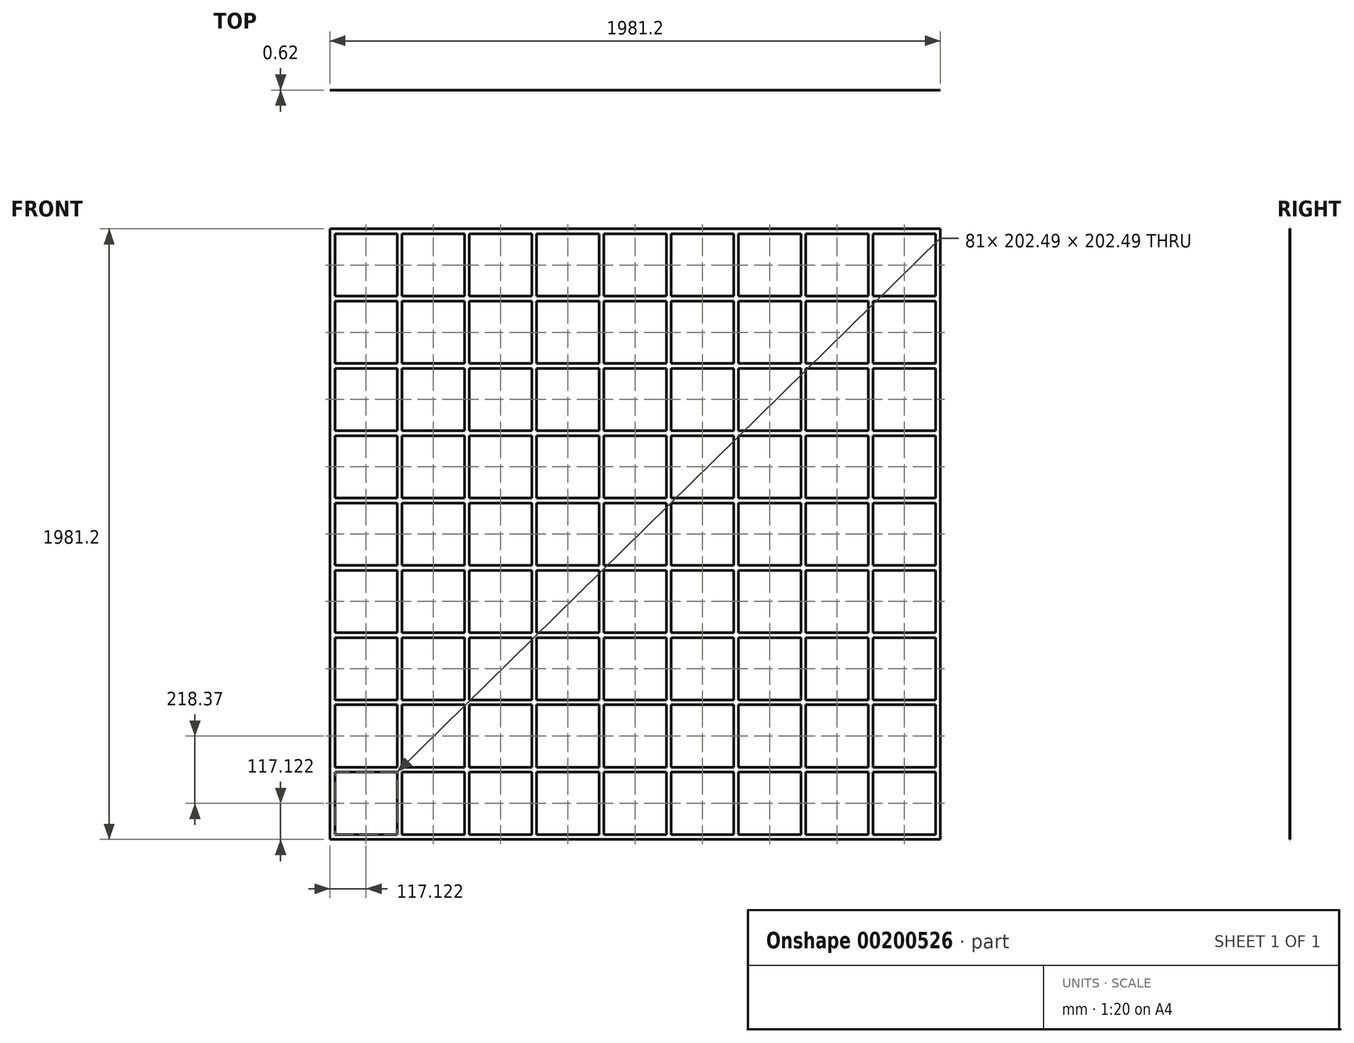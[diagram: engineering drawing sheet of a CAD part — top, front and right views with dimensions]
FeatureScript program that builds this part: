
annotation { "Feature Type Name" : "Feature", "Feature Type Description" : "" }
export const myFeature = defineFeature(function(context is Context, id is Id, definition is map)
    precondition{}
    {
        {
            assignVariable(context, id + "F0", {"name" : "Diameter", "anyValue" : 5 / 8});
        }
        {
            var Q0;
            Q0=qCreatedBy(makeId("Front.planeOp"),FACE);
            var sketch = newSketch(context, id + "F1", { "sketchPlane" : qUnion([Q0])});
            skLineSegment(sketch, "E0.bottom", {"start": v(-1066.8, 1066.8) * mm, "end": v(1066.8, 1066.8) * mm, "construction": true});
            skLineSegment(sketch, "E0.top", {"start": v(-1066.8, -1066.8) * mm, "end": v(1066.8, -1066.8) * mm, "construction": true});
            skLineSegment(sketch, "E0.left", {"start": v(-1066.8, 1066.8) * mm, "end": v(-1066.8, -1066.8) * mm, "construction": true});
            skLineSegment(sketch, "E0.right", {"start": v(1066.8, 1066.8) * mm, "end": v(1066.8, -1066.8) * mm, "construction": true});
            skLineSegment(sketch, "E1", {"start": v(1066.8, 0) * mm, "end": v(-1066.8, 0) * mm, "construction": true});
            skLineSegment(sketch, "E2", {"start": v(0, -1066.8) * mm, "end": v(0, 1066.8) * mm, "construction": true});
            skLineSegment(sketch, "E3.bottom", {"start": v(-990.6, 990.6) * mm, "end": v(990.6, 990.6) * mm, "construction": true});
            skLineSegment(sketch, "E3.top", {"start": v(-990.6, -990.6) * mm, "end": v(990.6, -990.6) * mm, "construction": true});
            skLineSegment(sketch, "E3.left", {"start": v(-990.6, 990.6) * mm, "end": v(-990.6, -990.6) * mm, "construction": true});
            skLineSegment(sketch, "E3.right", {"start": v(990.6, 990.6) * mm, "end": v(990.6, -990.6) * mm, "construction": true});
            skLineSegment(sketch, "E4.bottom", {"start": v(-990.6, 990.6) * mm, "end": v(-974.72, 990.6) * mm});
            skLineSegment(sketch, "E4.top", {"start": v(-990.6, -990.6) * mm, "end": v(-974.72, -990.6) * mm});
            skLineSegment(sketch, "E4.left", {"start": v(-990.6, 990.6) * mm, "end": v(-990.6, -990.6) * mm});
            skLineSegment(sketch, "E4.right", {"start": v(-974.72, 990.6) * mm, "end": v(-974.72, -990.6) * mm});
            skLineSegment(sketch, "E5.bottom", {"start": v(-772.23, 990.6) * mm, "end": v(-756.36, 990.6) * mm});
            skLineSegment(sketch, "E5.top", {"start": v(-772.23, -990.6) * mm, "end": v(-756.36, -990.6) * mm});
            skLineSegment(sketch, "E5.left", {"start": v(-772.23, 990.6) * mm, "end": v(-772.23, -990.6) * mm});
            skLineSegment(sketch, "E5.right", {"start": v(-756.36, 990.6) * mm, "end": v(-756.36, -990.6) * mm});
            skLineSegment(sketch, "E6.bottom", {"start": v(-553.86, 990.6) * mm, "end": v(-537.99, 990.6) * mm});
            skLineSegment(sketch, "E6.top", {"start": v(-553.86, -990.6) * mm, "end": v(-537.99, -990.6) * mm});
            skLineSegment(sketch, "E6.left", {"start": v(-553.86, 990.6) * mm, "end": v(-553.86, -990.6) * mm});
            skLineSegment(sketch, "E6.right", {"start": v(-537.99, 990.6) * mm, "end": v(-537.99, -990.6) * mm});
            skLineSegment(sketch, "E7.bottom", {"start": v(-335.5, 990.6) * mm, "end": v(-319.62, 990.6) * mm});
            skLineSegment(sketch, "E7.top", {"start": v(-335.5, -990.6) * mm, "end": v(-319.62, -990.6) * mm});
            skLineSegment(sketch, "E7.left", {"start": v(-335.5, 990.6) * mm, "end": v(-335.5, -990.6) * mm});
            skLineSegment(sketch, "E7.right", {"start": v(-319.62, 990.6) * mm, "end": v(-319.62, -990.6) * mm});
            skLineSegment(sketch, "E8.bottom", {"start": v(101.25, 990.6) * mm, "end": v(117.12, 990.6) * mm});
            skLineSegment(sketch, "E8.top", {"start": v(101.25, -990.6) * mm, "end": v(117.12, -990.6) * mm});
            skLineSegment(sketch, "E8.left", {"start": v(101.25, 990.6) * mm, "end": v(101.25, -990.6) * mm});
            skLineSegment(sketch, "E8.right", {"start": v(117.12, 990.6) * mm, "end": v(117.12, -990.6) * mm});
            skLineSegment(sketch, "E9.bottom", {"start": v(319.62, 990.6) * mm, "end": v(335.5, 990.6) * mm});
            skLineSegment(sketch, "E9.top", {"start": v(319.62, -990.6) * mm, "end": v(335.5, -990.6) * mm});
            skLineSegment(sketch, "E9.left", {"start": v(319.62, 990.6) * mm, "end": v(319.62, -990.6) * mm});
            skLineSegment(sketch, "E9.right", {"start": v(335.5, 990.6) * mm, "end": v(335.5, -990.6) * mm});
            skLineSegment(sketch, "E10.bottom", {"start": v(537.99, 990.6) * mm, "end": v(553.86, 990.6) * mm});
            skLineSegment(sketch, "E10.top", {"start": v(537.99, -990.6) * mm, "end": v(553.86, -990.6) * mm});
            skLineSegment(sketch, "E10.left", {"start": v(537.99, 990.6) * mm, "end": v(537.99, -990.6) * mm});
            skLineSegment(sketch, "E10.right", {"start": v(553.86, 990.6) * mm, "end": v(553.86, -990.6) * mm});
            skLineSegment(sketch, "E11.bottom", {"start": v(990.6, 990.6) * mm, "end": v(974.73, 990.6) * mm});
            skLineSegment(sketch, "E11.top", {"start": v(990.6, -990.6) * mm, "end": v(974.73, -990.6) * mm});
            skLineSegment(sketch, "E11.left", {"start": v(990.6, 990.6) * mm, "end": v(990.6, -990.6) * mm});
            skLineSegment(sketch, "E11.right", {"start": v(974.73, 990.6) * mm, "end": v(974.73, -990.6) * mm});
            skLineSegment(sketch, "E12.bottom", {"start": v(772.23, 990.6) * mm, "end": v(756.36, 990.6) * mm});
            skLineSegment(sketch, "E12.top", {"start": v(772.23, -990.6) * mm, "end": v(756.36, -990.6) * mm});
            skLineSegment(sketch, "E12.left", {"start": v(772.23, 990.6) * mm, "end": v(772.23, -990.6) * mm});
            skLineSegment(sketch, "E12.right", {"start": v(756.36, 990.6) * mm, "end": v(756.36, -990.6) * mm});
            skLineSegment(sketch, "E13.bottom", {"start": v(-117.12, 990.6) * mm, "end": v(-101.25, 990.6) * mm});
            skLineSegment(sketch, "E13.top", {"start": v(-117.12, -990.6) * mm, "end": v(-101.25, -990.6) * mm});
            skLineSegment(sketch, "E13.left", {"start": v(-117.12, 990.6) * mm, "end": v(-117.12, -990.6) * mm});
            skLineSegment(sketch, "E13.right", {"start": v(-101.25, 990.6) * mm, "end": v(-101.25, -990.6) * mm});
            skLineSegment(sketch, "E14.bottom", {"start": v(-990.6, 990.6) * mm, "end": v(990.6, 990.6) * mm});
            skLineSegment(sketch, "E14.top", {"start": v(-990.6, 974.72) * mm, "end": v(990.6, 974.73) * mm});
            skLineSegment(sketch, "E14.left", {"start": v(-990.6, 990.6) * mm, "end": v(-990.6, 974.72) * mm});
            skLineSegment(sketch, "E14.right", {"start": v(990.6, 990.6) * mm, "end": v(990.6, 974.73) * mm});
            skLineSegment(sketch, "E15.bottom", {"start": v(-990.6, 553.86) * mm, "end": v(990.6, 553.86) * mm});
            skLineSegment(sketch, "E15.top", {"start": v(-990.6, 537.99) * mm, "end": v(990.6, 537.99) * mm});
            skLineSegment(sketch, "E15.left", {"start": v(-990.6, 553.86) * mm, "end": v(-990.6, 537.99) * mm});
            skLineSegment(sketch, "E15.right", {"start": v(990.6, 553.86) * mm, "end": v(990.6, 537.99) * mm});
            skLineSegment(sketch, "E16.bottom", {"start": v(990.6, 756.36) * mm, "end": v(-990.6, 756.36) * mm});
            skLineSegment(sketch, "E16.top", {"start": v(990.6, 772.23) * mm, "end": v(-990.6, 772.23) * mm});
            skLineSegment(sketch, "E16.left", {"start": v(990.6, 756.36) * mm, "end": v(990.6, 772.23) * mm});
            skLineSegment(sketch, "E16.right", {"start": v(-990.6, 756.36) * mm, "end": v(-990.6, 772.23) * mm});
            skLineSegment(sketch, "E17.bottom", {"start": v(-990.6, 335.5) * mm, "end": v(990.6, 335.5) * mm});
            skLineSegment(sketch, "E17.top", {"start": v(-990.6, 319.62) * mm, "end": v(990.6, 319.62) * mm});
            skLineSegment(sketch, "E17.left", {"start": v(-990.6, 335.5) * mm, "end": v(-990.6, 319.62) * mm});
            skLineSegment(sketch, "E17.right", {"start": v(990.6, 335.5) * mm, "end": v(990.6, 319.62) * mm});
            skLineSegment(sketch, "E18.bottom", {"start": v(-990.6, 117.12) * mm, "end": v(990.6, 117.12) * mm});
            skLineSegment(sketch, "E18.top", {"start": v(-990.6, 101.25) * mm, "end": v(990.6, 101.25) * mm});
            skLineSegment(sketch, "E18.left", {"start": v(-990.6, 117.12) * mm, "end": v(-990.6, 101.25) * mm});
            skLineSegment(sketch, "E18.right", {"start": v(990.6, 117.12) * mm, "end": v(990.6, 101.25) * mm});
            skLineSegment(sketch, "E19.bottom", {"start": v(-990.6, -101.25) * mm, "end": v(990.6, -101.25) * mm});
            skLineSegment(sketch, "E19.top", {"start": v(-990.6, -117.12) * mm, "end": v(990.6, -117.12) * mm});
            skLineSegment(sketch, "E19.left", {"start": v(-990.6, -101.25) * mm, "end": v(-990.6, -117.12) * mm});
            skLineSegment(sketch, "E19.right", {"start": v(990.6, -101.25) * mm, "end": v(990.6, -117.12) * mm});
            skLineSegment(sketch, "E20.bottom", {"start": v(990.6, -319.62) * mm, "end": v(-990.6, -319.62) * mm});
            skLineSegment(sketch, "E20.top", {"start": v(990.6, -335.5) * mm, "end": v(-990.6, -335.5) * mm});
            skLineSegment(sketch, "E20.left", {"start": v(990.6, -319.62) * mm, "end": v(990.6, -335.5) * mm});
            skLineSegment(sketch, "E20.right", {"start": v(-990.6, -319.62) * mm, "end": v(-990.6, -335.5) * mm});
            skLineSegment(sketch, "E21.bottom", {"start": v(-990.6, -537.99) * mm, "end": v(990.6, -537.99) * mm});
            skLineSegment(sketch, "E21.top", {"start": v(-990.6, -553.86) * mm, "end": v(990.6, -553.86) * mm});
            skLineSegment(sketch, "E21.left", {"start": v(-990.6, -537.99) * mm, "end": v(-990.6, -553.86) * mm});
            skLineSegment(sketch, "E21.right", {"start": v(990.6, -537.99) * mm, "end": v(990.6, -553.86) * mm});
            skLineSegment(sketch, "E22.bottom", {"start": v(990.6, -756.36) * mm, "end": v(-990.6, -756.36) * mm});
            skLineSegment(sketch, "E22.top", {"start": v(990.6, -772.23) * mm, "end": v(-990.6, -772.23) * mm});
            skLineSegment(sketch, "E22.left", {"start": v(990.6, -756.36) * mm, "end": v(990.6, -772.23) * mm});
            skLineSegment(sketch, "E22.right", {"start": v(-990.6, -756.36) * mm, "end": v(-990.6, -772.23) * mm});
            skLineSegment(sketch, "E23.bottom", {"start": v(-990.6, -990.6) * mm, "end": v(990.6, -990.6) * mm});
            skLineSegment(sketch, "E23.top", {"start": v(-990.6, -974.73) * mm, "end": v(990.6, -974.72) * mm});
            skLineSegment(sketch, "E23.left", {"start": v(-990.6, -990.6) * mm, "end": v(-990.6, -974.73) * mm});
            skLineSegment(sketch, "E23.right", {"start": v(990.6, -990.6) * mm, "end": v(990.6, -974.72) * mm});
            skSolve(sketch);
        }
        {
            var Q0;
            Q0 = qSketchRegion(id + "F1", true);
            var Q1;
            {var subQ0=sQuery(id+"F1.wireOp",EDGE,"E19.bottom");var subQ1=sQuery(id+"F1.wireOp",EDGE,"E4.right");var subQ2=makeQuery(id+"F1.imprint","INTERSECT",VERTEX,{"derivedFrom":[subQ1,subQ0]});Q1=makeQuery(id+"F1.imprint","IMPRINT",FACE,{"disambiguationData":[TD([[makeQuery(id+"F1.imprint","IMPRINT",EDGE,{"disambiguationData":[TD([[subQ2,-1.0]])],"derivedFrom":subQ1}),1.0]])]});}
            var Q2;
            {var subQ0=sQuery(id+"F1.wireOp",EDGE,"E20.bottom");var subQ1=sQuery(id+"F1.wireOp",EDGE,"E4.right");var subQ2=makeQuery(id+"F1.imprint","INTERSECT",VERTEX,{"derivedFrom":[subQ1,subQ0]});Q2=makeQuery(id+"F1.imprint","IMPRINT",FACE,{"disambiguationData":[TD([[makeQuery(id+"F1.imprint","IMPRINT",EDGE,{"disambiguationData":[TD([[subQ2,-1.0]])],"derivedFrom":subQ1}),1.0]])]});}
            var Q3;
            {var subQ0=sQuery(id+"F1.wireOp",EDGE,"E21.bottom");var subQ1=sQuery(id+"F1.wireOp",EDGE,"E4.right");var subQ2=makeQuery(id+"F1.imprint","INTERSECT",VERTEX,{"derivedFrom":[subQ1,subQ0]});Q3=makeQuery(id+"F1.imprint","IMPRINT",FACE,{"disambiguationData":[TD([[makeQuery(id+"F1.imprint","IMPRINT",EDGE,{"disambiguationData":[TD([[subQ2,-1.0]])],"derivedFrom":subQ1}),1.0]])]});}
            var Q4;
            {var subQ0=sQuery(id+"F1.wireOp",EDGE,"E22.bottom");var subQ1=sQuery(id+"F1.wireOp",EDGE,"E4.right");var subQ2=makeQuery(id+"F1.imprint","INTERSECT",VERTEX,{"derivedFrom":[subQ1,subQ0]});Q4=makeQuery(id+"F1.imprint","IMPRINT",FACE,{"disambiguationData":[TD([[makeQuery(id+"F1.imprint","IMPRINT",EDGE,{"disambiguationData":[TD([[subQ2,-1.0]])],"derivedFrom":subQ1}),1.0]])]});}
            var Q5;
            {var subQ0=sQuery(id+"F1.wireOp",EDGE,"E22.top");var subQ1=sQuery(id+"F1.wireOp",EDGE,"E5.left");var subQ2=makeQuery(id+"F1.imprint","INTERSECT",VERTEX,{"derivedFrom":[subQ1,subQ0]});Q5=makeQuery(id+"F1.imprint","IMPRINT",FACE,{"disambiguationData":[TD([[makeQuery(id+"F1.imprint","IMPRINT",EDGE,{"disambiguationData":[TD([[subQ2,-1.0]])],"derivedFrom":subQ1}),1.0]])]});}
            var Q6;
            {var subQ0=sQuery(id+"F1.wireOp",EDGE,"E22.top");var subQ1=sQuery(id+"F1.wireOp",EDGE,"E6.left");var subQ2=makeQuery(id+"F1.imprint","INTERSECT",VERTEX,{"derivedFrom":[subQ1,subQ0]});Q6=makeQuery(id+"F1.imprint","IMPRINT",FACE,{"disambiguationData":[TD([[makeQuery(id+"F1.imprint","IMPRINT",EDGE,{"disambiguationData":[TD([[subQ2,-1.0]])],"derivedFrom":subQ1}),1.0]])]});}
            var Q7;
            {var subQ0=sQuery(id+"F1.wireOp",EDGE,"E21.top");var subQ1=sQuery(id+"F1.wireOp",EDGE,"E6.left");var subQ2=makeQuery(id+"F1.imprint","INTERSECT",VERTEX,{"derivedFrom":[subQ1,subQ0]});Q7=makeQuery(id+"F1.imprint","IMPRINT",FACE,{"disambiguationData":[TD([[makeQuery(id+"F1.imprint","IMPRINT",EDGE,{"disambiguationData":[TD([[subQ2,-1.0]])],"derivedFrom":subQ1}),1.0]])]});}
            var Q8;
            {var subQ0=sQuery(id+"F1.wireOp",EDGE,"E22.bottom");var subQ1=sQuery(id+"F1.wireOp",EDGE,"E5.right");var subQ2=makeQuery(id+"F1.imprint","INTERSECT",VERTEX,{"derivedFrom":[subQ1,subQ0]});Q8=makeQuery(id+"F1.imprint","IMPRINT",FACE,{"disambiguationData":[TD([[makeQuery(id+"F1.imprint","IMPRINT",EDGE,{"disambiguationData":[TD([[subQ2,-1.0]])],"derivedFrom":subQ1}),1.0]])]});}
            var Q9;
            {var subQ0=sQuery(id+"F1.wireOp",EDGE,"E21.top");var subQ1=sQuery(id+"F1.wireOp",EDGE,"E5.left");var subQ2=makeQuery(id+"F1.imprint","INTERSECT",VERTEX,{"derivedFrom":[subQ1,subQ0]});Q9=makeQuery(id+"F1.imprint","IMPRINT",FACE,{"disambiguationData":[TD([[makeQuery(id+"F1.imprint","IMPRINT",EDGE,{"disambiguationData":[TD([[subQ2,-1.0]])],"derivedFrom":subQ1}),1.0]])]});}
            var Q10;
            {var subQ0=sQuery(id+"F1.wireOp",EDGE,"E20.top");var subQ1=sQuery(id+"F1.wireOp",EDGE,"E5.left");var subQ2=makeQuery(id+"F1.imprint","INTERSECT",VERTEX,{"derivedFrom":[subQ1,subQ0]});Q10=makeQuery(id+"F1.imprint","IMPRINT",FACE,{"disambiguationData":[TD([[makeQuery(id+"F1.imprint","IMPRINT",EDGE,{"disambiguationData":[TD([[subQ2,-1.0]])],"derivedFrom":subQ1}),1.0]])]});}
            var Q11;
            {var subQ0=sQuery(id+"F1.wireOp",EDGE,"E19.top");var subQ1=sQuery(id+"F1.wireOp",EDGE,"E5.left");var subQ2=makeQuery(id+"F1.imprint","INTERSECT",VERTEX,{"derivedFrom":[subQ1,subQ0]});Q11=makeQuery(id+"F1.imprint","IMPRINT",FACE,{"disambiguationData":[TD([[makeQuery(id+"F1.imprint","IMPRINT",EDGE,{"disambiguationData":[TD([[subQ2,-1.0]])],"derivedFrom":subQ1}),1.0]])]});}
            var Q12;
            {var subQ0=sQuery(id+"F1.wireOp",EDGE,"E17.top");var subQ1=sQuery(id+"F1.wireOp",EDGE,"E5.left");var subQ2=makeQuery(id+"F1.imprint","INTERSECT",VERTEX,{"derivedFrom":[subQ1,subQ0]});Q12=makeQuery(id+"F1.imprint","IMPRINT",FACE,{"disambiguationData":[TD([[makeQuery(id+"F1.imprint","IMPRINT",EDGE,{"disambiguationData":[TD([[subQ2,-1.0]])],"derivedFrom":subQ1}),1.0]])]});}
            var Q13;
            {var subQ0=sQuery(id+"F1.wireOp",EDGE,"E15.top");var subQ1=sQuery(id+"F1.wireOp",EDGE,"E5.left");var subQ2=makeQuery(id+"F1.imprint","INTERSECT",VERTEX,{"derivedFrom":[subQ1,subQ0]});Q13=makeQuery(id+"F1.imprint","IMPRINT",FACE,{"disambiguationData":[TD([[makeQuery(id+"F1.imprint","IMPRINT",EDGE,{"disambiguationData":[TD([[subQ2,-1.0]])],"derivedFrom":subQ1}),1.0]])]});}
            var Q14;
            {var subQ0=sQuery(id+"F1.wireOp",EDGE,"E18.bottom");var subQ1=sQuery(id+"F1.wireOp",EDGE,"E4.right");var subQ2=makeQuery(id+"F1.imprint","INTERSECT",VERTEX,{"derivedFrom":[subQ1,subQ0]});Q14=makeQuery(id+"F1.imprint","IMPRINT",FACE,{"disambiguationData":[TD([[makeQuery(id+"F1.imprint","IMPRINT",EDGE,{"disambiguationData":[TD([[subQ2,-1.0]])],"derivedFrom":subQ1}),1.0]])]});}
            var Q15;
            {var subQ0=sQuery(id+"F1.wireOp",EDGE,"E18.top");var subQ1=sQuery(id+"F1.wireOp",EDGE,"E5.left");var subQ2=makeQuery(id+"F1.imprint","INTERSECT",VERTEX,{"derivedFrom":[subQ1,subQ0]});Q15=makeQuery(id+"F1.imprint","IMPRINT",FACE,{"disambiguationData":[TD([[makeQuery(id+"F1.imprint","IMPRINT",EDGE,{"disambiguationData":[TD([[subQ2,-1.0]])],"derivedFrom":subQ1}),1.0]])]});}
            var Q16;
            {var subQ0=sQuery(id+"F1.wireOp",EDGE,"E18.bottom");var subQ1=sQuery(id+"F1.wireOp",EDGE,"E5.right");var subQ2=makeQuery(id+"F1.imprint","INTERSECT",VERTEX,{"derivedFrom":[subQ1,subQ0]});Q16=makeQuery(id+"F1.imprint","IMPRINT",FACE,{"disambiguationData":[TD([[makeQuery(id+"F1.imprint","IMPRINT",EDGE,{"disambiguationData":[TD([[subQ2,-1.0]])],"derivedFrom":subQ1}),1.0]])]});}
            var Q17;
            {var subQ0=sQuery(id+"F1.wireOp",EDGE,"E18.bottom");var subQ1=sQuery(id+"F1.wireOp",EDGE,"E6.right");var subQ2=makeQuery(id+"F1.imprint","INTERSECT",VERTEX,{"derivedFrom":[subQ1,subQ0]});Q17=makeQuery(id+"F1.imprint","IMPRINT",FACE,{"disambiguationData":[TD([[makeQuery(id+"F1.imprint","IMPRINT",EDGE,{"disambiguationData":[TD([[subQ2,-1.0]])],"derivedFrom":subQ1}),1.0]])]});}
            var Q18;
            {var subQ0=sQuery(id+"F1.wireOp",EDGE,"E17.top");var subQ1=sQuery(id+"F1.wireOp",EDGE,"E6.left");var subQ2=makeQuery(id+"F1.imprint","INTERSECT",VERTEX,{"derivedFrom":[subQ1,subQ0]});Q18=makeQuery(id+"F1.imprint","IMPRINT",FACE,{"disambiguationData":[TD([[makeQuery(id+"F1.imprint","IMPRINT",EDGE,{"disambiguationData":[TD([[subQ2,-1.0]])],"derivedFrom":subQ1}),1.0]])]});}
            var Q19;
            {var subQ0=sQuery(id+"F1.wireOp",EDGE,"E18.top");var subQ1=sQuery(id+"F1.wireOp",EDGE,"E6.left");var subQ2=makeQuery(id+"F1.imprint","INTERSECT",VERTEX,{"derivedFrom":[subQ1,subQ0]});Q19=makeQuery(id+"F1.imprint","IMPRINT",FACE,{"disambiguationData":[TD([[makeQuery(id+"F1.imprint","IMPRINT",EDGE,{"disambiguationData":[TD([[subQ2,-1.0]])],"derivedFrom":subQ1}),1.0]])]});}
            var Q20;
            {var subQ0=sQuery(id+"F1.wireOp",EDGE,"E18.bottom");var subQ1=sQuery(id+"F1.wireOp",EDGE,"E6.left");var subQ2=makeQuery(id+"F1.imprint","INTERSECT",VERTEX,{"derivedFrom":[subQ1,subQ0]});Q20=makeQuery(id+"F1.imprint","IMPRINT",FACE,{"disambiguationData":[TD([[makeQuery(id+"F1.imprint","IMPRINT",EDGE,{"disambiguationData":[TD([[subQ2,-1.0]])],"derivedFrom":subQ1}),1.0]])]});}
            var Q21;
            {var subQ0=sQuery(id+"F1.wireOp",EDGE,"E18.bottom");var subQ1=sQuery(id+"F1.wireOp",EDGE,"E5.left");var subQ2=makeQuery(id+"F1.imprint","INTERSECT",VERTEX,{"derivedFrom":[subQ1,subQ0]});Q21=makeQuery(id+"F1.imprint","IMPRINT",FACE,{"disambiguationData":[TD([[makeQuery(id+"F1.imprint","IMPRINT",EDGE,{"disambiguationData":[TD([[subQ2,-1.0]])],"derivedFrom":subQ1}),1.0]])]});}
            var Q22;
            {var subQ0=sQuery(id+"F1.wireOp",EDGE,"E19.bottom");var subQ1=sQuery(id+"F1.wireOp",EDGE,"E5.left");var subQ2=makeQuery(id+"F1.imprint","INTERSECT",VERTEX,{"derivedFrom":[subQ1,subQ0]});Q22=makeQuery(id+"F1.imprint","IMPRINT",FACE,{"disambiguationData":[TD([[makeQuery(id+"F1.imprint","IMPRINT",EDGE,{"disambiguationData":[TD([[subQ2,-1.0]])],"derivedFrom":subQ1}),1.0]])]});}
            var Q23;
            {var subQ0=sQuery(id+"F1.wireOp",EDGE,"E17.bottom");var subQ1=sQuery(id+"F1.wireOp",EDGE,"E5.left");var subQ2=makeQuery(id+"F1.imprint","INTERSECT",VERTEX,{"derivedFrom":[subQ1,subQ0]});Q23=makeQuery(id+"F1.imprint","IMPRINT",FACE,{"disambiguationData":[TD([[makeQuery(id+"F1.imprint","IMPRINT",EDGE,{"disambiguationData":[TD([[subQ2,-1.0]])],"derivedFrom":subQ1}),1.0]])]});}
            var Q24;
            {var subQ0=sQuery(id+"F1.wireOp",EDGE,"E17.bottom");var subQ1=sQuery(id+"F1.wireOp",EDGE,"E6.left");var subQ2=makeQuery(id+"F1.imprint","INTERSECT",VERTEX,{"derivedFrom":[subQ1,subQ0]});Q24=makeQuery(id+"F1.imprint","IMPRINT",FACE,{"disambiguationData":[TD([[makeQuery(id+"F1.imprint","IMPRINT",EDGE,{"disambiguationData":[TD([[subQ2,-1.0]])],"derivedFrom":subQ1}),1.0]])]});}
            var Q25;
            {var subQ0=sQuery(id+"F1.wireOp",EDGE,"E17.bottom");var subQ1=sQuery(id+"F1.wireOp",EDGE,"E7.left");var subQ2=makeQuery(id+"F1.imprint","INTERSECT",VERTEX,{"derivedFrom":[subQ1,subQ0]});Q25=makeQuery(id+"F1.imprint","IMPRINT",FACE,{"disambiguationData":[TD([[makeQuery(id+"F1.imprint","IMPRINT",EDGE,{"disambiguationData":[TD([[subQ2,-1.0]])],"derivedFrom":subQ1}),1.0]])]});}
            var Q26;
            {var subQ0=sQuery(id+"F1.wireOp",EDGE,"E17.top");var subQ1=sQuery(id+"F1.wireOp",EDGE,"E7.left");var subQ2=makeQuery(id+"F1.imprint","INTERSECT",VERTEX,{"derivedFrom":[subQ1,subQ0]});Q26=makeQuery(id+"F1.imprint","IMPRINT",FACE,{"disambiguationData":[TD([[makeQuery(id+"F1.imprint","IMPRINT",EDGE,{"disambiguationData":[TD([[subQ2,-1.0]])],"derivedFrom":subQ1}),1.0]])]});}
            var Q27;
            {var subQ0=sQuery(id+"F1.wireOp",EDGE,"E18.bottom");var subQ1=sQuery(id+"F1.wireOp",EDGE,"E7.left");var subQ2=makeQuery(id+"F1.imprint","INTERSECT",VERTEX,{"derivedFrom":[subQ1,subQ0]});Q27=makeQuery(id+"F1.imprint","IMPRINT",FACE,{"disambiguationData":[TD([[makeQuery(id+"F1.imprint","IMPRINT",EDGE,{"disambiguationData":[TD([[subQ2,-1.0]])],"derivedFrom":subQ1}),1.0]])]});}
            var Q28;
            {var subQ0=sQuery(id+"F1.wireOp",EDGE,"E18.top");var subQ1=sQuery(id+"F1.wireOp",EDGE,"E7.left");var subQ2=makeQuery(id+"F1.imprint","INTERSECT",VERTEX,{"derivedFrom":[subQ1,subQ0]});Q28=makeQuery(id+"F1.imprint","IMPRINT",FACE,{"disambiguationData":[TD([[makeQuery(id+"F1.imprint","IMPRINT",EDGE,{"disambiguationData":[TD([[subQ2,-1.0]])],"derivedFrom":subQ1}),1.0]])]});}
            var Q29;
            {var subQ0=sQuery(id+"F1.wireOp",EDGE,"E19.bottom");var subQ1=sQuery(id+"F1.wireOp",EDGE,"E7.left");var subQ2=makeQuery(id+"F1.imprint","INTERSECT",VERTEX,{"derivedFrom":[subQ1,subQ0]});Q29=makeQuery(id+"F1.imprint","IMPRINT",FACE,{"disambiguationData":[TD([[makeQuery(id+"F1.imprint","IMPRINT",EDGE,{"disambiguationData":[TD([[subQ2,-1.0]])],"derivedFrom":subQ1}),1.0]])]});}
            var Q30;
            {var subQ0=sQuery(id+"F1.wireOp",EDGE,"E19.bottom");var subQ1=sQuery(id+"F1.wireOp",EDGE,"E6.right");var subQ2=makeQuery(id+"F1.imprint","INTERSECT",VERTEX,{"derivedFrom":[subQ1,subQ0]});Q30=makeQuery(id+"F1.imprint","IMPRINT",FACE,{"disambiguationData":[TD([[makeQuery(id+"F1.imprint","IMPRINT",EDGE,{"disambiguationData":[TD([[subQ2,-1.0]])],"derivedFrom":subQ1}),1.0]])]});}
            var Q31;
            {var subQ0=sQuery(id+"F1.wireOp",EDGE,"E19.bottom");var subQ1=sQuery(id+"F1.wireOp",EDGE,"E6.left");var subQ2=makeQuery(id+"F1.imprint","INTERSECT",VERTEX,{"derivedFrom":[subQ1,subQ0]});Q31=makeQuery(id+"F1.imprint","IMPRINT",FACE,{"disambiguationData":[TD([[makeQuery(id+"F1.imprint","IMPRINT",EDGE,{"disambiguationData":[TD([[subQ2,-1.0]])],"derivedFrom":subQ1}),1.0]])]});}
            var Q32;
            {var subQ0=sQuery(id+"F1.wireOp",EDGE,"E19.bottom");var subQ1=sQuery(id+"F1.wireOp",EDGE,"E5.right");var subQ2=makeQuery(id+"F1.imprint","INTERSECT",VERTEX,{"derivedFrom":[subQ1,subQ0]});Q32=makeQuery(id+"F1.imprint","IMPRINT",FACE,{"disambiguationData":[TD([[makeQuery(id+"F1.imprint","IMPRINT",EDGE,{"disambiguationData":[TD([[subQ2,-1.0]])],"derivedFrom":subQ1}),1.0]])]});}
            var Q33;
            {var subQ0=sQuery(id+"F1.wireOp",EDGE,"E19.top");var subQ1=sQuery(id+"F1.wireOp",EDGE,"E6.left");var subQ2=makeQuery(id+"F1.imprint","INTERSECT",VERTEX,{"derivedFrom":[subQ1,subQ0]});Q33=makeQuery(id+"F1.imprint","IMPRINT",FACE,{"disambiguationData":[TD([[makeQuery(id+"F1.imprint","IMPRINT",EDGE,{"disambiguationData":[TD([[subQ2,-1.0]])],"derivedFrom":subQ1}),1.0]])]});}
            var Q34;
            {var subQ0=sQuery(id+"F1.wireOp",EDGE,"E17.bottom");var subQ1=sQuery(id+"F1.wireOp",EDGE,"E4.right");var subQ2=makeQuery(id+"F1.imprint","INTERSECT",VERTEX,{"derivedFrom":[subQ1,subQ0]});Q34=makeQuery(id+"F1.imprint","IMPRINT",FACE,{"disambiguationData":[TD([[makeQuery(id+"F1.imprint","IMPRINT",EDGE,{"disambiguationData":[TD([[subQ2,-1.0]])],"derivedFrom":subQ1}),1.0]])]});}
            var Q35;
            {var subQ0=sQuery(id+"F1.wireOp",EDGE,"E17.bottom");var subQ1=sQuery(id+"F1.wireOp",EDGE,"E5.right");var subQ2=makeQuery(id+"F1.imprint","INTERSECT",VERTEX,{"derivedFrom":[subQ1,subQ0]});Q35=makeQuery(id+"F1.imprint","IMPRINT",FACE,{"disambiguationData":[TD([[makeQuery(id+"F1.imprint","IMPRINT",EDGE,{"disambiguationData":[TD([[subQ2,-1.0]])],"derivedFrom":subQ1}),1.0]])]});}
            var Q36;
            {var subQ0=sQuery(id+"F1.wireOp",EDGE,"E15.top");var subQ1=sQuery(id+"F1.wireOp",EDGE,"E6.left");var subQ2=makeQuery(id+"F1.imprint","INTERSECT",VERTEX,{"derivedFrom":[subQ1,subQ0]});Q36=makeQuery(id+"F1.imprint","IMPRINT",FACE,{"disambiguationData":[TD([[makeQuery(id+"F1.imprint","IMPRINT",EDGE,{"disambiguationData":[TD([[subQ2,-1.0]])],"derivedFrom":subQ1}),1.0]])]});}
            var Q37;
            {var subQ0=sQuery(id+"F1.wireOp",EDGE,"E17.bottom");var subQ1=sQuery(id+"F1.wireOp",EDGE,"E6.right");var subQ2=makeQuery(id+"F1.imprint","INTERSECT",VERTEX,{"derivedFrom":[subQ1,subQ0]});Q37=makeQuery(id+"F1.imprint","IMPRINT",FACE,{"disambiguationData":[TD([[makeQuery(id+"F1.imprint","IMPRINT",EDGE,{"disambiguationData":[TD([[subQ2,-1.0]])],"derivedFrom":subQ1}),1.0]])]});}
            var Q38;
            {var subQ0=sQuery(id+"F1.wireOp",EDGE,"E15.top");var subQ1=sQuery(id+"F1.wireOp",EDGE,"E7.left");var subQ2=makeQuery(id+"F1.imprint","INTERSECT",VERTEX,{"derivedFrom":[subQ1,subQ0]});Q38=makeQuery(id+"F1.imprint","IMPRINT",FACE,{"disambiguationData":[TD([[makeQuery(id+"F1.imprint","IMPRINT",EDGE,{"disambiguationData":[TD([[subQ2,-1.0]])],"derivedFrom":subQ1}),1.0]])]});}
            var Q39;
            {var subQ0=sQuery(id+"F1.wireOp",EDGE,"E15.bottom");var subQ1=sQuery(id+"F1.wireOp",EDGE,"E7.left");var subQ2=makeQuery(id+"F1.imprint","INTERSECT",VERTEX,{"derivedFrom":[subQ1,subQ0]});Q39=makeQuery(id+"F1.imprint","IMPRINT",FACE,{"disambiguationData":[TD([[makeQuery(id+"F1.imprint","IMPRINT",EDGE,{"disambiguationData":[TD([[subQ2,-1.0]])],"derivedFrom":subQ1}),1.0]])]});}
            var Q40;
            {var subQ0=sQuery(id+"F1.wireOp",EDGE,"E15.bottom");var subQ1=sQuery(id+"F1.wireOp",EDGE,"E6.right");var subQ2=makeQuery(id+"F1.imprint","INTERSECT",VERTEX,{"derivedFrom":[subQ1,subQ0]});Q40=makeQuery(id+"F1.imprint","IMPRINT",FACE,{"disambiguationData":[TD([[makeQuery(id+"F1.imprint","IMPRINT",EDGE,{"disambiguationData":[TD([[subQ2,-1.0]])],"derivedFrom":subQ1}),1.0]])]});}
            var Q41;
            {var subQ0=sQuery(id+"F1.wireOp",EDGE,"E15.bottom");var subQ1=sQuery(id+"F1.wireOp",EDGE,"E6.left");var subQ2=makeQuery(id+"F1.imprint","INTERSECT",VERTEX,{"derivedFrom":[subQ1,subQ0]});Q41=makeQuery(id+"F1.imprint","IMPRINT",FACE,{"disambiguationData":[TD([[makeQuery(id+"F1.imprint","IMPRINT",EDGE,{"disambiguationData":[TD([[subQ2,-1.0]])],"derivedFrom":subQ1}),1.0]])]});}
            var Q42;
            {var subQ0=sQuery(id+"F1.wireOp",EDGE,"E15.bottom");var subQ1=sQuery(id+"F1.wireOp",EDGE,"E5.right");var subQ2=makeQuery(id+"F1.imprint","INTERSECT",VERTEX,{"derivedFrom":[subQ1,subQ0]});Q42=makeQuery(id+"F1.imprint","IMPRINT",FACE,{"disambiguationData":[TD([[makeQuery(id+"F1.imprint","IMPRINT",EDGE,{"disambiguationData":[TD([[subQ2,-1.0]])],"derivedFrom":subQ1}),1.0]])]});}
            var Q43;
            {var subQ0=sQuery(id+"F1.wireOp",EDGE,"E15.bottom");var subQ1=sQuery(id+"F1.wireOp",EDGE,"E4.right");var subQ2=makeQuery(id+"F1.imprint","INTERSECT",VERTEX,{"derivedFrom":[subQ1,subQ0]});Q43=makeQuery(id+"F1.imprint","IMPRINT",FACE,{"disambiguationData":[TD([[makeQuery(id+"F1.imprint","IMPRINT",EDGE,{"disambiguationData":[TD([[subQ2,-1.0]])],"derivedFrom":subQ1}),1.0]])]});}
            var Q44;
            {var subQ0=sQuery(id+"F1.wireOp",EDGE,"E15.bottom");var subQ1=sQuery(id+"F1.wireOp",EDGE,"E5.left");var subQ2=makeQuery(id+"F1.imprint","INTERSECT",VERTEX,{"derivedFrom":[subQ1,subQ0]});Q44=makeQuery(id+"F1.imprint","IMPRINT",FACE,{"disambiguationData":[TD([[makeQuery(id+"F1.imprint","IMPRINT",EDGE,{"disambiguationData":[TD([[subQ2,-1.0]])],"derivedFrom":subQ1}),1.0]])]});}
            var Q45;
            {var subQ0=sQuery(id+"F1.wireOp",EDGE,"E16.bottom");var subQ1=sQuery(id+"F1.wireOp",EDGE,"E5.left");var subQ2=makeQuery(id+"F1.imprint","INTERSECT",VERTEX,{"derivedFrom":[subQ1,subQ0]});Q45=makeQuery(id+"F1.imprint","IMPRINT",FACE,{"disambiguationData":[TD([[makeQuery(id+"F1.imprint","IMPRINT",EDGE,{"disambiguationData":[TD([[subQ2,-1.0]])],"derivedFrom":subQ1}),1.0]])]});}
            var Q46;
            {var subQ0=sQuery(id+"F1.wireOp",EDGE,"E16.bottom");var subQ1=sQuery(id+"F1.wireOp",EDGE,"E6.left");var subQ2=makeQuery(id+"F1.imprint","INTERSECT",VERTEX,{"derivedFrom":[subQ1,subQ0]});Q46=makeQuery(id+"F1.imprint","IMPRINT",FACE,{"disambiguationData":[TD([[makeQuery(id+"F1.imprint","IMPRINT",EDGE,{"disambiguationData":[TD([[subQ2,-1.0]])],"derivedFrom":subQ1}),1.0]])]});}
            var Q47;
            {var subQ0=sQuery(id+"F1.wireOp",EDGE,"E16.bottom");var subQ1=sQuery(id+"F1.wireOp",EDGE,"E7.left");var subQ2=makeQuery(id+"F1.imprint","INTERSECT",VERTEX,{"derivedFrom":[subQ1,subQ0]});Q47=makeQuery(id+"F1.imprint","IMPRINT",FACE,{"disambiguationData":[TD([[makeQuery(id+"F1.imprint","IMPRINT",EDGE,{"disambiguationData":[TD([[subQ2,-1.0]])],"derivedFrom":subQ1}),1.0]])]});}
            var Q48;
            {var subQ0=sQuery(id+"F1.wireOp",EDGE,"E15.bottom");var subQ1=sQuery(id+"F1.wireOp",EDGE,"E7.right");var subQ2=makeQuery(id+"F1.imprint","INTERSECT",VERTEX,{"derivedFrom":[subQ1,subQ0]});Q48=makeQuery(id+"F1.imprint","IMPRINT",FACE,{"disambiguationData":[TD([[makeQuery(id+"F1.imprint","IMPRINT",EDGE,{"disambiguationData":[TD([[subQ2,-1.0]])],"derivedFrom":subQ1}),1.0]])]});}
            var Q49;
            {var subQ0=sQuery(id+"F1.wireOp",EDGE,"E17.bottom");var subQ1=sQuery(id+"F1.wireOp",EDGE,"E7.right");var subQ2=makeQuery(id+"F1.imprint","INTERSECT",VERTEX,{"derivedFrom":[subQ1,subQ0]});Q49=makeQuery(id+"F1.imprint","IMPRINT",FACE,{"disambiguationData":[TD([[makeQuery(id+"F1.imprint","IMPRINT",EDGE,{"disambiguationData":[TD([[subQ2,-1.0]])],"derivedFrom":subQ1}),1.0]])]});}
            var Q50;
            {var subQ0=sQuery(id+"F1.wireOp",EDGE,"E18.bottom");var subQ1=sQuery(id+"F1.wireOp",EDGE,"E7.right");var subQ2=makeQuery(id+"F1.imprint","INTERSECT",VERTEX,{"derivedFrom":[subQ1,subQ0]});Q50=makeQuery(id+"F1.imprint","IMPRINT",FACE,{"disambiguationData":[TD([[makeQuery(id+"F1.imprint","IMPRINT",EDGE,{"disambiguationData":[TD([[subQ2,-1.0]])],"derivedFrom":subQ1}),1.0]])]});}
            var Q51;
            {var subQ0=sQuery(id+"F1.wireOp",EDGE,"E17.top");var subQ1=sQuery(id+"F1.wireOp",EDGE,"E13.left");var subQ2=makeQuery(id+"F1.imprint","INTERSECT",VERTEX,{"derivedFrom":[subQ1,subQ0]});Q51=makeQuery(id+"F1.imprint","IMPRINT",FACE,{"disambiguationData":[TD([[makeQuery(id+"F1.imprint","IMPRINT",EDGE,{"disambiguationData":[TD([[subQ2,-1.0]])],"derivedFrom":subQ1}),1.0]])]});}
            var Q52;
            {var subQ0=sQuery(id+"F1.wireOp",EDGE,"E18.bottom");var subQ1=sQuery(id+"F1.wireOp",EDGE,"E13.left");var subQ2=makeQuery(id+"F1.imprint","INTERSECT",VERTEX,{"derivedFrom":[subQ1,subQ0]});Q52=makeQuery(id+"F1.imprint","IMPRINT",FACE,{"disambiguationData":[TD([[makeQuery(id+"F1.imprint","IMPRINT",EDGE,{"disambiguationData":[TD([[subQ2,-1.0]])],"derivedFrom":subQ1}),1.0]])]});}
            var Q53;
            {var subQ0=sQuery(id+"F1.wireOp",EDGE,"E17.bottom");var subQ1=sQuery(id+"F1.wireOp",EDGE,"E13.left");var subQ2=makeQuery(id+"F1.imprint","INTERSECT",VERTEX,{"derivedFrom":[subQ1,subQ0]});Q53=makeQuery(id+"F1.imprint","IMPRINT",FACE,{"disambiguationData":[TD([[makeQuery(id+"F1.imprint","IMPRINT",EDGE,{"disambiguationData":[TD([[subQ2,-1.0]])],"derivedFrom":subQ1}),1.0]])]});}
            var Q54;
            {var subQ0=sQuery(id+"F1.wireOp",EDGE,"E15.bottom");var subQ1=sQuery(id+"F1.wireOp",EDGE,"E13.left");var subQ2=makeQuery(id+"F1.imprint","INTERSECT",VERTEX,{"derivedFrom":[subQ1,subQ0]});Q54=makeQuery(id+"F1.imprint","IMPRINT",FACE,{"disambiguationData":[TD([[makeQuery(id+"F1.imprint","IMPRINT",EDGE,{"disambiguationData":[TD([[subQ2,-1.0]])],"derivedFrom":subQ1}),1.0]])]});}
            var Q55;
            {var subQ0=sQuery(id+"F1.wireOp",EDGE,"E16.top");var subQ1=sQuery(id+"F1.wireOp",EDGE,"E13.left");var subQ2=makeQuery(id+"F1.imprint","INTERSECT",VERTEX,{"derivedFrom":[subQ1,subQ0]});Q55=makeQuery(id+"F1.imprint","IMPRINT",FACE,{"disambiguationData":[TD([[makeQuery(id+"F1.imprint","IMPRINT",EDGE,{"disambiguationData":[TD([[subQ2,-1.0]])],"derivedFrom":subQ1}),1.0]])]});}
            var Q56;
            {var subQ0=sQuery(id+"F1.wireOp",EDGE,"E16.bottom");var subQ1=sQuery(id+"F1.wireOp",EDGE,"E13.left");var subQ2=makeQuery(id+"F1.imprint","INTERSECT",VERTEX,{"derivedFrom":[subQ1,subQ0]});Q56=makeQuery(id+"F1.imprint","IMPRINT",FACE,{"disambiguationData":[TD([[makeQuery(id+"F1.imprint","IMPRINT",EDGE,{"disambiguationData":[TD([[subQ2,-1.0]])],"derivedFrom":subQ1}),1.0]])]});}
            var Q57;
            {var subQ0=sQuery(id+"F1.wireOp",EDGE,"E16.top");var subQ1=sQuery(id+"F1.wireOp",EDGE,"E7.right");var subQ2=makeQuery(id+"F1.imprint","INTERSECT",VERTEX,{"derivedFrom":[subQ1,subQ0]});Q57=makeQuery(id+"F1.imprint","IMPRINT",FACE,{"disambiguationData":[TD([[makeQuery(id+"F1.imprint","IMPRINT",EDGE,{"disambiguationData":[TD([[subQ2,-1.0]])],"derivedFrom":subQ1}),1.0]])]});}
            var Q58;
            {var subQ0=sQuery(id+"F1.wireOp",EDGE,"E16.top");var subQ1=sQuery(id+"F1.wireOp",EDGE,"E7.left");var subQ2=makeQuery(id+"F1.imprint","INTERSECT",VERTEX,{"derivedFrom":[subQ1,subQ0]});Q58=makeQuery(id+"F1.imprint","IMPRINT",FACE,{"disambiguationData":[TD([[makeQuery(id+"F1.imprint","IMPRINT",EDGE,{"disambiguationData":[TD([[subQ2,-1.0]])],"derivedFrom":subQ1}),1.0]])]});}
            var Q59;
            {var subQ0=sQuery(id+"F1.wireOp",EDGE,"E16.top");var subQ1=sQuery(id+"F1.wireOp",EDGE,"E6.right");var subQ2=makeQuery(id+"F1.imprint","INTERSECT",VERTEX,{"derivedFrom":[subQ1,subQ0]});Q59=makeQuery(id+"F1.imprint","IMPRINT",FACE,{"disambiguationData":[TD([[makeQuery(id+"F1.imprint","IMPRINT",EDGE,{"disambiguationData":[TD([[subQ2,-1.0]])],"derivedFrom":subQ1}),1.0]])]});}
            var Q60;
            {var subQ0=sQuery(id+"F1.wireOp",EDGE,"E16.top");var subQ1=sQuery(id+"F1.wireOp",EDGE,"E6.left");var subQ2=makeQuery(id+"F1.imprint","INTERSECT",VERTEX,{"derivedFrom":[subQ1,subQ0]});Q60=makeQuery(id+"F1.imprint","IMPRINT",FACE,{"disambiguationData":[TD([[makeQuery(id+"F1.imprint","IMPRINT",EDGE,{"disambiguationData":[TD([[subQ2,-1.0]])],"derivedFrom":subQ1}),1.0]])]});}
            var Q61;
            {var subQ0=sQuery(id+"F1.wireOp",EDGE,"E16.top");var subQ1=sQuery(id+"F1.wireOp",EDGE,"E5.right");var subQ2=makeQuery(id+"F1.imprint","INTERSECT",VERTEX,{"derivedFrom":[subQ1,subQ0]});Q61=makeQuery(id+"F1.imprint","IMPRINT",FACE,{"disambiguationData":[TD([[makeQuery(id+"F1.imprint","IMPRINT",EDGE,{"disambiguationData":[TD([[subQ2,-1.0]])],"derivedFrom":subQ1}),1.0]])]});}
            var Q62;
            {var subQ0=sQuery(id+"F1.wireOp",EDGE,"E17.bottom");var subQ1=sQuery(id+"F1.wireOp",EDGE,"E8.left");var subQ2=makeQuery(id+"F1.imprint","INTERSECT",VERTEX,{"derivedFrom":[subQ1,subQ0]});Q62=makeQuery(id+"F1.imprint","IMPRINT",FACE,{"disambiguationData":[TD([[makeQuery(id+"F1.imprint","IMPRINT",EDGE,{"disambiguationData":[TD([[subQ2,-1.0]])],"derivedFrom":subQ1}),-1.0]])]});}
            var Q63;
            {var subQ0=sQuery(id+"F1.wireOp",EDGE,"E17.bottom");var subQ1=sQuery(id+"F1.wireOp",EDGE,"E8.right");var subQ2=makeQuery(id+"F1.imprint","INTERSECT",VERTEX,{"derivedFrom":[subQ1,subQ0]});Q63=makeQuery(id+"F1.imprint","IMPRINT",FACE,{"disambiguationData":[TD([[makeQuery(id+"F1.imprint","IMPRINT",EDGE,{"disambiguationData":[TD([[subQ2,-1.0]])],"derivedFrom":subQ1}),1.0]])]});}
            var Q64;
            {var subQ0=sQuery(id+"F1.wireOp",EDGE,"E17.bottom");var subQ1=sQuery(id+"F1.wireOp",EDGE,"E8.left");var subQ2=makeQuery(id+"F1.imprint","INTERSECT",VERTEX,{"derivedFrom":[subQ1,subQ0]});Q64=makeQuery(id+"F1.imprint","IMPRINT",FACE,{"disambiguationData":[TD([[makeQuery(id+"F1.imprint","IMPRINT",EDGE,{"disambiguationData":[TD([[subQ2,-1.0]])],"derivedFrom":subQ1}),1.0]])]});}
            var Q65;
            {var subQ0=sQuery(id+"F1.wireOp",EDGE,"E17.top");var subQ1=sQuery(id+"F1.wireOp",EDGE,"E8.left");var subQ2=makeQuery(id+"F1.imprint","INTERSECT",VERTEX,{"derivedFrom":[subQ1,subQ0]});Q65=makeQuery(id+"F1.imprint","IMPRINT",FACE,{"disambiguationData":[TD([[makeQuery(id+"F1.imprint","IMPRINT",EDGE,{"disambiguationData":[TD([[subQ2,-1.0]])],"derivedFrom":subQ1}),1.0]])]});}
            var Q66;
            {var subQ0=sQuery(id+"F1.wireOp",EDGE,"E18.bottom");var subQ1=sQuery(id+"F1.wireOp",EDGE,"E8.left");var subQ2=makeQuery(id+"F1.imprint","INTERSECT",VERTEX,{"derivedFrom":[subQ1,subQ0]});Q66=makeQuery(id+"F1.imprint","IMPRINT",FACE,{"disambiguationData":[TD([[makeQuery(id+"F1.imprint","IMPRINT",EDGE,{"disambiguationData":[TD([[subQ2,-1.0]])],"derivedFrom":subQ1}),1.0]])]});}
            var Q67;
            {var subQ0=sQuery(id+"F1.wireOp",EDGE,"E18.bottom");var subQ1=sQuery(id+"F1.wireOp",EDGE,"E8.left");var subQ2=makeQuery(id+"F1.imprint","INTERSECT",VERTEX,{"derivedFrom":[subQ1,subQ0]});Q67=makeQuery(id+"F1.imprint","IMPRINT",FACE,{"disambiguationData":[TD([[makeQuery(id+"F1.imprint","IMPRINT",EDGE,{"disambiguationData":[TD([[subQ2,-1.0]])],"derivedFrom":subQ1}),-1.0]])]});}
            var Q68;
            {var subQ0=sQuery(id+"F1.wireOp",EDGE,"E18.top");var subQ1=sQuery(id+"F1.wireOp",EDGE,"E8.left");var subQ2=makeQuery(id+"F1.imprint","INTERSECT",VERTEX,{"derivedFrom":[subQ1,subQ0]});Q68=makeQuery(id+"F1.imprint","IMPRINT",FACE,{"disambiguationData":[TD([[makeQuery(id+"F1.imprint","IMPRINT",EDGE,{"disambiguationData":[TD([[subQ2,-1.0]])],"derivedFrom":subQ1}),1.0]])]});}
            var Q69;
            {var subQ0=sQuery(id+"F1.wireOp",EDGE,"E18.bottom");var subQ1=sQuery(id+"F1.wireOp",EDGE,"E8.right");var subQ2=makeQuery(id+"F1.imprint","INTERSECT",VERTEX,{"derivedFrom":[subQ1,subQ0]});Q69=makeQuery(id+"F1.imprint","IMPRINT",FACE,{"disambiguationData":[TD([[makeQuery(id+"F1.imprint","IMPRINT",EDGE,{"disambiguationData":[TD([[subQ2,-1.0]])],"derivedFrom":subQ1}),1.0]])]});}
            var Q70;
            {var subQ0=sQuery(id+"F1.wireOp",EDGE,"E17.top");var subQ1=sQuery(id+"F1.wireOp",EDGE,"E9.left");var subQ2=makeQuery(id+"F1.imprint","INTERSECT",VERTEX,{"derivedFrom":[subQ1,subQ0]});Q70=makeQuery(id+"F1.imprint","IMPRINT",FACE,{"disambiguationData":[TD([[makeQuery(id+"F1.imprint","IMPRINT",EDGE,{"disambiguationData":[TD([[subQ2,-1.0]])],"derivedFrom":subQ1}),1.0]])]});}
            var Q71;
            {var subQ0=sQuery(id+"F1.wireOp",EDGE,"E18.bottom");var subQ1=sQuery(id+"F1.wireOp",EDGE,"E9.left");var subQ2=makeQuery(id+"F1.imprint","INTERSECT",VERTEX,{"derivedFrom":[subQ1,subQ0]});Q71=makeQuery(id+"F1.imprint","IMPRINT",FACE,{"disambiguationData":[TD([[makeQuery(id+"F1.imprint","IMPRINT",EDGE,{"disambiguationData":[TD([[subQ2,-1.0]])],"derivedFrom":subQ1}),1.0]])]});}
            var Q72;
            {var subQ0=sQuery(id+"F1.wireOp",EDGE,"E18.top");var subQ1=sQuery(id+"F1.wireOp",EDGE,"E9.left");var subQ2=makeQuery(id+"F1.imprint","INTERSECT",VERTEX,{"derivedFrom":[subQ1,subQ0]});Q72=makeQuery(id+"F1.imprint","IMPRINT",FACE,{"disambiguationData":[TD([[makeQuery(id+"F1.imprint","IMPRINT",EDGE,{"disambiguationData":[TD([[subQ2,-1.0]])],"derivedFrom":subQ1}),1.0]])]});}
            var Q73;
            {var subQ0=sQuery(id+"F1.wireOp",EDGE,"E18.bottom");var subQ1=sQuery(id+"F1.wireOp",EDGE,"E9.right");var subQ2=makeQuery(id+"F1.imprint","INTERSECT",VERTEX,{"derivedFrom":[subQ1,subQ0]});Q73=makeQuery(id+"F1.imprint","IMPRINT",FACE,{"disambiguationData":[TD([[makeQuery(id+"F1.imprint","IMPRINT",EDGE,{"disambiguationData":[TD([[subQ2,-1.0]])],"derivedFrom":subQ1}),1.0]])]});}
            var Q74;
            {var subQ0=sQuery(id+"F1.wireOp",EDGE,"E17.top");var subQ1=sQuery(id+"F1.wireOp",EDGE,"E10.left");var subQ2=makeQuery(id+"F1.imprint","INTERSECT",VERTEX,{"derivedFrom":[subQ1,subQ0]});Q74=makeQuery(id+"F1.imprint","IMPRINT",FACE,{"disambiguationData":[TD([[makeQuery(id+"F1.imprint","IMPRINT",EDGE,{"disambiguationData":[TD([[subQ2,-1.0]])],"derivedFrom":subQ1}),1.0]])]});}
            var Q75;
            {var subQ0=sQuery(id+"F1.wireOp",EDGE,"E18.bottom");var subQ1=sQuery(id+"F1.wireOp",EDGE,"E10.left");var subQ2=makeQuery(id+"F1.imprint","INTERSECT",VERTEX,{"derivedFrom":[subQ1,subQ0]});Q75=makeQuery(id+"F1.imprint","IMPRINT",FACE,{"disambiguationData":[TD([[makeQuery(id+"F1.imprint","IMPRINT",EDGE,{"disambiguationData":[TD([[subQ2,-1.0]])],"derivedFrom":subQ1}),1.0]])]});}
            var Q76;
            {var subQ0=sQuery(id+"F1.wireOp",EDGE,"E18.top");var subQ1=sQuery(id+"F1.wireOp",EDGE,"E10.left");var subQ2=makeQuery(id+"F1.imprint","INTERSECT",VERTEX,{"derivedFrom":[subQ1,subQ0]});Q76=makeQuery(id+"F1.imprint","IMPRINT",FACE,{"disambiguationData":[TD([[makeQuery(id+"F1.imprint","IMPRINT",EDGE,{"disambiguationData":[TD([[subQ2,-1.0]])],"derivedFrom":subQ1}),1.0]])]});}
            var Q77;
            {var subQ0=sQuery(id+"F1.wireOp",EDGE,"E18.bottom");var subQ1=sQuery(id+"F1.wireOp",EDGE,"E10.right");var subQ2=makeQuery(id+"F1.imprint","INTERSECT",VERTEX,{"derivedFrom":[subQ1,subQ0]});Q77=makeQuery(id+"F1.imprint","IMPRINT",FACE,{"disambiguationData":[TD([[makeQuery(id+"F1.imprint","IMPRINT",EDGE,{"disambiguationData":[TD([[subQ2,-1.0]])],"derivedFrom":subQ1}),1.0]])]});}
            var Q78;
            {var subQ0=sQuery(id+"F1.wireOp",EDGE,"E17.bottom");var subQ1=sQuery(id+"F1.wireOp",EDGE,"E10.right");var subQ2=makeQuery(id+"F1.imprint","INTERSECT",VERTEX,{"derivedFrom":[subQ1,subQ0]});Q78=makeQuery(id+"F1.imprint","IMPRINT",FACE,{"disambiguationData":[TD([[makeQuery(id+"F1.imprint","IMPRINT",EDGE,{"disambiguationData":[TD([[subQ2,-1.0]])],"derivedFrom":subQ1}),1.0]])]});}
            var Q79;
            {var subQ0=sQuery(id+"F1.wireOp",EDGE,"E17.bottom");var subQ1=sQuery(id+"F1.wireOp",EDGE,"E9.right");var subQ2=makeQuery(id+"F1.imprint","INTERSECT",VERTEX,{"derivedFrom":[subQ1,subQ0]});Q79=makeQuery(id+"F1.imprint","IMPRINT",FACE,{"disambiguationData":[TD([[makeQuery(id+"F1.imprint","IMPRINT",EDGE,{"disambiguationData":[TD([[subQ2,-1.0]])],"derivedFrom":subQ1}),1.0]])]});}
            var Q80;
            {var subQ0=sQuery(id+"F1.wireOp",EDGE,"E17.bottom");var subQ1=sQuery(id+"F1.wireOp",EDGE,"E10.left");var subQ2=makeQuery(id+"F1.imprint","INTERSECT",VERTEX,{"derivedFrom":[subQ1,subQ0]});Q80=makeQuery(id+"F1.imprint","IMPRINT",FACE,{"disambiguationData":[TD([[makeQuery(id+"F1.imprint","IMPRINT",EDGE,{"disambiguationData":[TD([[subQ2,-1.0]])],"derivedFrom":subQ1}),1.0]])]});}
            var Q81;
            {var subQ0=sQuery(id+"F1.wireOp",EDGE,"E15.top");var subQ1=sQuery(id+"F1.wireOp",EDGE,"E10.left");var subQ2=makeQuery(id+"F1.imprint","INTERSECT",VERTEX,{"derivedFrom":[subQ1,subQ0]});Q81=makeQuery(id+"F1.imprint","IMPRINT",FACE,{"disambiguationData":[TD([[makeQuery(id+"F1.imprint","IMPRINT",EDGE,{"disambiguationData":[TD([[subQ2,-1.0]])],"derivedFrom":subQ1}),1.0]])]});}
            var Q82;
            {var subQ0=sQuery(id+"F1.wireOp",EDGE,"E15.bottom");var subQ1=sQuery(id+"F1.wireOp",EDGE,"E9.right");var subQ2=makeQuery(id+"F1.imprint","INTERSECT",VERTEX,{"derivedFrom":[subQ1,subQ0]});Q82=makeQuery(id+"F1.imprint","IMPRINT",FACE,{"disambiguationData":[TD([[makeQuery(id+"F1.imprint","IMPRINT",EDGE,{"disambiguationData":[TD([[subQ2,-1.0]])],"derivedFrom":subQ1}),1.0]])]});}
            var Q83;
            {var subQ0=sQuery(id+"F1.wireOp",EDGE,"E15.top");var subQ1=sQuery(id+"F1.wireOp",EDGE,"E13.left");var subQ2=makeQuery(id+"F1.imprint","INTERSECT",VERTEX,{"derivedFrom":[subQ1,subQ0]});Q83=makeQuery(id+"F1.imprint","IMPRINT",FACE,{"disambiguationData":[TD([[makeQuery(id+"F1.imprint","IMPRINT",EDGE,{"disambiguationData":[TD([[subQ2,-1.0]])],"derivedFrom":subQ1}),1.0]])]});}
            var Q84;
            {var subQ0=sQuery(id+"F1.wireOp",EDGE,"E15.bottom");var subQ1=sQuery(id+"F1.wireOp",EDGE,"E8.left");var subQ2=makeQuery(id+"F1.imprint","INTERSECT",VERTEX,{"derivedFrom":[subQ1,subQ0]});Q84=makeQuery(id+"F1.imprint","IMPRINT",FACE,{"disambiguationData":[TD([[makeQuery(id+"F1.imprint","IMPRINT",EDGE,{"disambiguationData":[TD([[subQ2,-1.0]])],"derivedFrom":subQ1}),-1.0]])]});}
            var Q85;
            {var subQ0=sQuery(id+"F1.wireOp",EDGE,"E16.top");var subQ1=sQuery(id+"F1.wireOp",EDGE,"E8.left");var subQ2=makeQuery(id+"F1.imprint","INTERSECT",VERTEX,{"derivedFrom":[subQ1,subQ0]});Q85=makeQuery(id+"F1.imprint","IMPRINT",FACE,{"disambiguationData":[TD([[makeQuery(id+"F1.imprint","IMPRINT",EDGE,{"disambiguationData":[TD([[subQ2,-1.0]])],"derivedFrom":subQ1}),-1.0]])]});}
            var Q86;
            {var subQ0=sQuery(id+"F1.wireOp",EDGE,"E16.top");var subQ1=sQuery(id+"F1.wireOp",EDGE,"E8.left");var subQ2=makeQuery(id+"F1.imprint","INTERSECT",VERTEX,{"derivedFrom":[subQ1,subQ0]});Q86=makeQuery(id+"F1.imprint","IMPRINT",FACE,{"disambiguationData":[TD([[makeQuery(id+"F1.imprint","IMPRINT",EDGE,{"disambiguationData":[TD([[subQ2,-1.0]])],"derivedFrom":subQ1}),1.0]])]});}
            var Q87;
            {var subQ0=sQuery(id+"F1.wireOp",EDGE,"E14.top");var subQ1=sQuery(id+"F1.wireOp",EDGE,"E8.left");var subQ2=makeQuery(id+"F1.imprint","INTERSECT",VERTEX,{"derivedFrom":[subQ1,subQ0]});Q87=makeQuery(id+"F1.imprint","IMPRINT",FACE,{"disambiguationData":[TD([[makeQuery(id+"F1.imprint","IMPRINT",EDGE,{"disambiguationData":[TD([[subQ2,-1.0]])],"derivedFrom":subQ1}),1.0]])]});}
            var Q88;
            {var subQ0=sQuery(id+"F1.wireOp",EDGE,"E16.bottom");var subQ1=sQuery(id+"F1.wireOp",EDGE,"E8.left");var subQ2=makeQuery(id+"F1.imprint","INTERSECT",VERTEX,{"derivedFrom":[subQ1,subQ0]});Q88=makeQuery(id+"F1.imprint","IMPRINT",FACE,{"disambiguationData":[TD([[makeQuery(id+"F1.imprint","IMPRINT",EDGE,{"disambiguationData":[TD([[subQ2,-1.0]])],"derivedFrom":subQ1}),1.0]])]});}
            var Q89;
            {var subQ0=sQuery(id+"F1.wireOp",EDGE,"E15.bottom");var subQ1=sQuery(id+"F1.wireOp",EDGE,"E8.right");var subQ2=makeQuery(id+"F1.imprint","INTERSECT",VERTEX,{"derivedFrom":[subQ1,subQ0]});Q89=makeQuery(id+"F1.imprint","IMPRINT",FACE,{"disambiguationData":[TD([[makeQuery(id+"F1.imprint","IMPRINT",EDGE,{"disambiguationData":[TD([[subQ2,-1.0]])],"derivedFrom":subQ1}),1.0]])]});}
            var Q90;
            {var subQ0=sQuery(id+"F1.wireOp",EDGE,"E15.bottom");var subQ1=sQuery(id+"F1.wireOp",EDGE,"E8.left");var subQ2=makeQuery(id+"F1.imprint","INTERSECT",VERTEX,{"derivedFrom":[subQ1,subQ0]});Q90=makeQuery(id+"F1.imprint","IMPRINT",FACE,{"disambiguationData":[TD([[makeQuery(id+"F1.imprint","IMPRINT",EDGE,{"disambiguationData":[TD([[subQ2,-1.0]])],"derivedFrom":subQ1}),1.0]])]});}
            var Q91;
            {var subQ0=sQuery(id+"F1.wireOp",EDGE,"E15.top");var subQ1=sQuery(id+"F1.wireOp",EDGE,"E8.left");var subQ2=makeQuery(id+"F1.imprint","INTERSECT",VERTEX,{"derivedFrom":[subQ1,subQ0]});Q91=makeQuery(id+"F1.imprint","IMPRINT",FACE,{"disambiguationData":[TD([[makeQuery(id+"F1.imprint","IMPRINT",EDGE,{"disambiguationData":[TD([[subQ2,-1.0]])],"derivedFrom":subQ1}),1.0]])]});}
            var Q92;
            {var subQ0=sQuery(id+"F1.wireOp",EDGE,"E17.bottom");var subQ1=sQuery(id+"F1.wireOp",EDGE,"E9.left");var subQ2=makeQuery(id+"F1.imprint","INTERSECT",VERTEX,{"derivedFrom":[subQ1,subQ0]});Q92=makeQuery(id+"F1.imprint","IMPRINT",FACE,{"disambiguationData":[TD([[makeQuery(id+"F1.imprint","IMPRINT",EDGE,{"disambiguationData":[TD([[subQ2,-1.0]])],"derivedFrom":subQ1}),1.0]])]});}
            var Q93;
            {var subQ0=sQuery(id+"F1.wireOp",EDGE,"E19.bottom");var subQ1=sQuery(id+"F1.wireOp",EDGE,"E7.right");var subQ2=makeQuery(id+"F1.imprint","INTERSECT",VERTEX,{"derivedFrom":[subQ1,subQ0]});Q93=makeQuery(id+"F1.imprint","IMPRINT",FACE,{"disambiguationData":[TD([[makeQuery(id+"F1.imprint","IMPRINT",EDGE,{"disambiguationData":[TD([[subQ2,-1.0]])],"derivedFrom":subQ1}),1.0]])]});}
            var Q94;
            {var subQ0=sQuery(id+"F1.wireOp",EDGE,"E19.bottom");var subQ1=sQuery(id+"F1.wireOp",EDGE,"E13.left");var subQ2=makeQuery(id+"F1.imprint","INTERSECT",VERTEX,{"derivedFrom":[subQ1,subQ0]});Q94=makeQuery(id+"F1.imprint","IMPRINT",FACE,{"disambiguationData":[TD([[makeQuery(id+"F1.imprint","IMPRINT",EDGE,{"disambiguationData":[TD([[subQ2,-1.0]])],"derivedFrom":subQ1}),1.0]])]});}
            var Q95;
            {var subQ0=sQuery(id+"F1.wireOp",EDGE,"E18.top");var subQ1=sQuery(id+"F1.wireOp",EDGE,"E13.left");var subQ2=makeQuery(id+"F1.imprint","INTERSECT",VERTEX,{"derivedFrom":[subQ1,subQ0]});Q95=makeQuery(id+"F1.imprint","IMPRINT",FACE,{"disambiguationData":[TD([[makeQuery(id+"F1.imprint","IMPRINT",EDGE,{"disambiguationData":[TD([[subQ2,-1.0]])],"derivedFrom":subQ1}),1.0]])]});}
            var Q96;
            {var subQ0=sQuery(id+"F1.wireOp",EDGE,"E19.bottom");var subQ1=sQuery(id+"F1.wireOp",EDGE,"E8.left");var subQ2=makeQuery(id+"F1.imprint","INTERSECT",VERTEX,{"derivedFrom":[subQ1,subQ0]});Q96=makeQuery(id+"F1.imprint","IMPRINT",FACE,{"disambiguationData":[TD([[makeQuery(id+"F1.imprint","IMPRINT",EDGE,{"disambiguationData":[TD([[subQ2,-1.0]])],"derivedFrom":subQ1}),-1.0]])]});}
            var Q97;
            {var subQ0=sQuery(id+"F1.wireOp",EDGE,"E19.bottom");var subQ1=sQuery(id+"F1.wireOp",EDGE,"E8.left");var subQ2=makeQuery(id+"F1.imprint","INTERSECT",VERTEX,{"derivedFrom":[subQ1,subQ0]});Q97=makeQuery(id+"F1.imprint","IMPRINT",FACE,{"disambiguationData":[TD([[makeQuery(id+"F1.imprint","IMPRINT",EDGE,{"disambiguationData":[TD([[subQ2,-1.0]])],"derivedFrom":subQ1}),1.0]])]});}
            var Q98;
            {var subQ0=sQuery(id+"F1.wireOp",EDGE,"E16.top");var subQ1=sQuery(id+"F1.wireOp",EDGE,"E4.right");var subQ2=makeQuery(id+"F1.imprint","INTERSECT",VERTEX,{"derivedFrom":[subQ1,subQ0]});Q98=makeQuery(id+"F1.imprint","IMPRINT",FACE,{"disambiguationData":[TD([[makeQuery(id+"F1.imprint","IMPRINT",EDGE,{"disambiguationData":[TD([[subQ2,-1.0]])],"derivedFrom":subQ1}),1.0]])]});}
            var Q99;
            {var subQ0=sQuery(id+"F1.wireOp",EDGE,"E16.top");var subQ1=sQuery(id+"F1.wireOp",EDGE,"E5.left");var subQ2=makeQuery(id+"F1.imprint","INTERSECT",VERTEX,{"derivedFrom":[subQ1,subQ0]});Q99=makeQuery(id+"F1.imprint","IMPRINT",FACE,{"disambiguationData":[TD([[makeQuery(id+"F1.imprint","IMPRINT",EDGE,{"disambiguationData":[TD([[subQ2,-1.0]])],"derivedFrom":subQ1}),1.0]])]});}
            var Q100;
            {var subQ0=sQuery(id+"F1.wireOp",EDGE,"E14.top");var subQ1=sQuery(id+"F1.wireOp",EDGE,"E5.left");var subQ2=makeQuery(id+"F1.imprint","INTERSECT",VERTEX,{"derivedFrom":[subQ1,subQ0]});Q100=makeQuery(id+"F1.imprint","IMPRINT",FACE,{"disambiguationData":[TD([[makeQuery(id+"F1.imprint","IMPRINT",EDGE,{"disambiguationData":[TD([[subQ2,-1.0]])],"derivedFrom":subQ1}),1.0]])]});}
            var Q101;
            {var subQ0=sQuery(id+"F1.wireOp",EDGE,"E14.top");var subQ1=sQuery(id+"F1.wireOp",EDGE,"E6.left");var subQ2=makeQuery(id+"F1.imprint","INTERSECT",VERTEX,{"derivedFrom":[subQ1,subQ0]});Q101=makeQuery(id+"F1.imprint","IMPRINT",FACE,{"disambiguationData":[TD([[makeQuery(id+"F1.imprint","IMPRINT",EDGE,{"disambiguationData":[TD([[subQ2,-1.0]])],"derivedFrom":subQ1}),1.0]])]});}
            var Q102;
            {var subQ0=sQuery(id+"F1.wireOp",EDGE,"E14.top");var subQ1=sQuery(id+"F1.wireOp",EDGE,"E7.left");var subQ2=makeQuery(id+"F1.imprint","INTERSECT",VERTEX,{"derivedFrom":[subQ1,subQ0]});Q102=makeQuery(id+"F1.imprint","IMPRINT",FACE,{"disambiguationData":[TD([[makeQuery(id+"F1.imprint","IMPRINT",EDGE,{"disambiguationData":[TD([[subQ2,-1.0]])],"derivedFrom":subQ1}),1.0]])]});}
            var Q103;
            {var subQ0=sQuery(id+"F1.wireOp",EDGE,"E16.top");var subQ1=sQuery(id+"F1.wireOp",EDGE,"E8.right");var subQ2=makeQuery(id+"F1.imprint","INTERSECT",VERTEX,{"derivedFrom":[subQ1,subQ0]});Q103=makeQuery(id+"F1.imprint","IMPRINT",FACE,{"disambiguationData":[TD([[makeQuery(id+"F1.imprint","IMPRINT",EDGE,{"disambiguationData":[TD([[subQ2,-1.0]])],"derivedFrom":subQ1}),1.0]])]});}
            var Q104;
            {var subQ0=sQuery(id+"F1.wireOp",EDGE,"E14.top");var subQ1=sQuery(id+"F1.wireOp",EDGE,"E9.left");var subQ2=makeQuery(id+"F1.imprint","INTERSECT",VERTEX,{"derivedFrom":[subQ1,subQ0]});Q104=makeQuery(id+"F1.imprint","IMPRINT",FACE,{"disambiguationData":[TD([[makeQuery(id+"F1.imprint","IMPRINT",EDGE,{"disambiguationData":[TD([[subQ2,-1.0]])],"derivedFrom":subQ1}),1.0]])]});}
            var Q105;
            {var subQ0=sQuery(id+"F1.wireOp",EDGE,"E16.bottom");var subQ1=sQuery(id+"F1.wireOp",EDGE,"E9.left");var subQ2=makeQuery(id+"F1.imprint","INTERSECT",VERTEX,{"derivedFrom":[subQ1,subQ0]});Q105=makeQuery(id+"F1.imprint","IMPRINT",FACE,{"disambiguationData":[TD([[makeQuery(id+"F1.imprint","IMPRINT",EDGE,{"disambiguationData":[TD([[subQ2,-1.0]])],"derivedFrom":subQ1}),1.0]])]});}
            var Q106;
            {var subQ0=sQuery(id+"F1.wireOp",EDGE,"E15.top");var subQ1=sQuery(id+"F1.wireOp",EDGE,"E9.left");var subQ2=makeQuery(id+"F1.imprint","INTERSECT",VERTEX,{"derivedFrom":[subQ1,subQ0]});Q106=makeQuery(id+"F1.imprint","IMPRINT",FACE,{"disambiguationData":[TD([[makeQuery(id+"F1.imprint","IMPRINT",EDGE,{"disambiguationData":[TD([[subQ2,-1.0]])],"derivedFrom":subQ1}),1.0]])]});}
            var Q107;
            {var subQ0=sQuery(id+"F1.wireOp",EDGE,"E16.bottom");var subQ1=sQuery(id+"F1.wireOp",EDGE,"E10.left");var subQ2=makeQuery(id+"F1.imprint","INTERSECT",VERTEX,{"derivedFrom":[subQ1,subQ0]});Q107=makeQuery(id+"F1.imprint","IMPRINT",FACE,{"disambiguationData":[TD([[makeQuery(id+"F1.imprint","IMPRINT",EDGE,{"disambiguationData":[TD([[subQ2,-1.0]])],"derivedFrom":subQ1}),1.0]])]});}
            var Q108;
            {var subQ0=sQuery(id+"F1.wireOp",EDGE,"E15.bottom");var subQ1=sQuery(id+"F1.wireOp",EDGE,"E10.right");var subQ2=makeQuery(id+"F1.imprint","INTERSECT",VERTEX,{"derivedFrom":[subQ1,subQ0]});Q108=makeQuery(id+"F1.imprint","IMPRINT",FACE,{"disambiguationData":[TD([[makeQuery(id+"F1.imprint","IMPRINT",EDGE,{"disambiguationData":[TD([[subQ2,-1.0]])],"derivedFrom":subQ1}),1.0]])]});}
            var Q109;
            {var subQ0=sQuery(id+"F1.wireOp",EDGE,"E15.bottom");var subQ1=sQuery(id+"F1.wireOp",EDGE,"E10.left");var subQ2=makeQuery(id+"F1.imprint","INTERSECT",VERTEX,{"derivedFrom":[subQ1,subQ0]});Q109=makeQuery(id+"F1.imprint","IMPRINT",FACE,{"disambiguationData":[TD([[makeQuery(id+"F1.imprint","IMPRINT",EDGE,{"disambiguationData":[TD([[subQ2,-1.0]])],"derivedFrom":subQ1}),1.0]])]});}
            var Q110;
            {var subQ0=sQuery(id+"F1.wireOp",EDGE,"E15.bottom");var subQ1=sQuery(id+"F1.wireOp",EDGE,"E9.left");var subQ2=makeQuery(id+"F1.imprint","INTERSECT",VERTEX,{"derivedFrom":[subQ1,subQ0]});Q110=makeQuery(id+"F1.imprint","IMPRINT",FACE,{"disambiguationData":[TD([[makeQuery(id+"F1.imprint","IMPRINT",EDGE,{"disambiguationData":[TD([[subQ2,-1.0]])],"derivedFrom":subQ1}),1.0]])]});}
            var Q111;
            {var subQ0=sQuery(id+"F1.wireOp",EDGE,"E15.bottom");var subQ1=sQuery(id+"F1.wireOp",EDGE,"E12.left");var subQ2=makeQuery(id+"F1.imprint","INTERSECT",VERTEX,{"derivedFrom":[subQ1,subQ0]});Q111=makeQuery(id+"F1.imprint","IMPRINT",FACE,{"disambiguationData":[TD([[makeQuery(id+"F1.imprint","IMPRINT",EDGE,{"disambiguationData":[TD([[subQ2,-1.0]])],"derivedFrom":subQ1}),-1.0]])]});}
            var Q112;
            {var subQ0=sQuery(id+"F1.wireOp",EDGE,"E16.bottom");var subQ1=sQuery(id+"F1.wireOp",EDGE,"E12.left");var subQ2=makeQuery(id+"F1.imprint","INTERSECT",VERTEX,{"derivedFrom":[subQ1,subQ0]});Q112=makeQuery(id+"F1.imprint","IMPRINT",FACE,{"disambiguationData":[TD([[makeQuery(id+"F1.imprint","IMPRINT",EDGE,{"disambiguationData":[TD([[subQ2,-1.0]])],"derivedFrom":subQ1}),-1.0]])]});}
            var Q113;
            {var subQ0=sQuery(id+"F1.wireOp",EDGE,"E16.top");var subQ1=sQuery(id+"F1.wireOp",EDGE,"E10.right");var subQ2=makeQuery(id+"F1.imprint","INTERSECT",VERTEX,{"derivedFrom":[subQ1,subQ0]});Q113=makeQuery(id+"F1.imprint","IMPRINT",FACE,{"disambiguationData":[TD([[makeQuery(id+"F1.imprint","IMPRINT",EDGE,{"disambiguationData":[TD([[subQ2,-1.0]])],"derivedFrom":subQ1}),1.0]])]});}
            var Q114;
            {var subQ0=sQuery(id+"F1.wireOp",EDGE,"E16.top");var subQ1=sQuery(id+"F1.wireOp",EDGE,"E12.left");var subQ2=makeQuery(id+"F1.imprint","INTERSECT",VERTEX,{"derivedFrom":[subQ1,subQ0]});Q114=makeQuery(id+"F1.imprint","IMPRINT",FACE,{"disambiguationData":[TD([[makeQuery(id+"F1.imprint","IMPRINT",EDGE,{"disambiguationData":[TD([[subQ2,-1.0]])],"derivedFrom":subQ1}),-1.0]])]});}
            var Q115;
            {var subQ0=sQuery(id+"F1.wireOp",EDGE,"E18.bottom");var subQ1=sQuery(id+"F1.wireOp",EDGE,"E11.right");var subQ2=makeQuery(id+"F1.imprint","INTERSECT",VERTEX,{"derivedFrom":[subQ1,subQ0]});Q115=makeQuery(id+"F1.imprint","IMPRINT",FACE,{"disambiguationData":[TD([[makeQuery(id+"F1.imprint","IMPRINT",EDGE,{"disambiguationData":[TD([[subQ2,-1.0]])],"derivedFrom":subQ1}),-1.0]])]});}
            var Q116;
            {var subQ0=sQuery(id+"F1.wireOp",EDGE,"E18.top");var subQ1=sQuery(id+"F1.wireOp",EDGE,"E12.left");var subQ2=makeQuery(id+"F1.imprint","INTERSECT",VERTEX,{"derivedFrom":[subQ1,subQ0]});Q116=makeQuery(id+"F1.imprint","IMPRINT",FACE,{"disambiguationData":[TD([[makeQuery(id+"F1.imprint","IMPRINT",EDGE,{"disambiguationData":[TD([[subQ2,-1.0]])],"derivedFrom":subQ1}),-1.0]])]});}
            var Q117;
            {var subQ0=sQuery(id+"F1.wireOp",EDGE,"E19.bottom");var subQ1=sQuery(id+"F1.wireOp",EDGE,"E10.right");var subQ2=makeQuery(id+"F1.imprint","INTERSECT",VERTEX,{"derivedFrom":[subQ1,subQ0]});Q117=makeQuery(id+"F1.imprint","IMPRINT",FACE,{"disambiguationData":[TD([[makeQuery(id+"F1.imprint","IMPRINT",EDGE,{"disambiguationData":[TD([[subQ2,-1.0]])],"derivedFrom":subQ1}),1.0]])]});}
            var Q118;
            {var subQ0=sQuery(id+"F1.wireOp",EDGE,"E19.bottom");var subQ1=sQuery(id+"F1.wireOp",EDGE,"E12.left");var subQ2=makeQuery(id+"F1.imprint","INTERSECT",VERTEX,{"derivedFrom":[subQ1,subQ0]});Q118=makeQuery(id+"F1.imprint","IMPRINT",FACE,{"disambiguationData":[TD([[makeQuery(id+"F1.imprint","IMPRINT",EDGE,{"disambiguationData":[TD([[subQ2,-1.0]])],"derivedFrom":subQ1}),-1.0]])]});}
            var Q119;
            {var subQ0=sQuery(id+"F1.wireOp",EDGE,"E19.bottom");var subQ1=sQuery(id+"F1.wireOp",EDGE,"E11.right");var subQ2=makeQuery(id+"F1.imprint","INTERSECT",VERTEX,{"derivedFrom":[subQ1,subQ0]});Q119=makeQuery(id+"F1.imprint","IMPRINT",FACE,{"disambiguationData":[TD([[makeQuery(id+"F1.imprint","IMPRINT",EDGE,{"disambiguationData":[TD([[subQ2,-1.0]])],"derivedFrom":subQ1}),-1.0]])]});}
            var Q120;
            {var subQ0=sQuery(id+"F1.wireOp",EDGE,"E19.top");var subQ1=sQuery(id+"F1.wireOp",EDGE,"E12.left");var subQ2=makeQuery(id+"F1.imprint","INTERSECT",VERTEX,{"derivedFrom":[subQ1,subQ0]});Q120=makeQuery(id+"F1.imprint","IMPRINT",FACE,{"disambiguationData":[TD([[makeQuery(id+"F1.imprint","IMPRINT",EDGE,{"disambiguationData":[TD([[subQ2,-1.0]])],"derivedFrom":subQ1}),-1.0]])]});}
            var Q121;
            {var subQ0=sQuery(id+"F1.wireOp",EDGE,"E19.bottom");var subQ1=sQuery(id+"F1.wireOp",EDGE,"E9.right");var subQ2=makeQuery(id+"F1.imprint","INTERSECT",VERTEX,{"derivedFrom":[subQ1,subQ0]});Q121=makeQuery(id+"F1.imprint","IMPRINT",FACE,{"disambiguationData":[TD([[makeQuery(id+"F1.imprint","IMPRINT",EDGE,{"disambiguationData":[TD([[subQ2,-1.0]])],"derivedFrom":subQ1}),1.0]])]});}
            var Q122;
            {var subQ0=sQuery(id+"F1.wireOp",EDGE,"E19.bottom");var subQ1=sQuery(id+"F1.wireOp",EDGE,"E10.left");var subQ2=makeQuery(id+"F1.imprint","INTERSECT",VERTEX,{"derivedFrom":[subQ1,subQ0]});Q122=makeQuery(id+"F1.imprint","IMPRINT",FACE,{"disambiguationData":[TD([[makeQuery(id+"F1.imprint","IMPRINT",EDGE,{"disambiguationData":[TD([[subQ2,-1.0]])],"derivedFrom":subQ1}),1.0]])]});}
            var Q123;
            {var subQ0=sQuery(id+"F1.wireOp",EDGE,"E19.top");var subQ1=sQuery(id+"F1.wireOp",EDGE,"E10.left");var subQ2=makeQuery(id+"F1.imprint","INTERSECT",VERTEX,{"derivedFrom":[subQ1,subQ0]});Q123=makeQuery(id+"F1.imprint","IMPRINT",FACE,{"disambiguationData":[TD([[makeQuery(id+"F1.imprint","IMPRINT",EDGE,{"disambiguationData":[TD([[subQ2,-1.0]])],"derivedFrom":subQ1}),1.0]])]});}
            var Q124;
            {var subQ0=sQuery(id+"F1.wireOp",EDGE,"E20.bottom");var subQ1=sQuery(id+"F1.wireOp",EDGE,"E10.right");var subQ2=makeQuery(id+"F1.imprint","INTERSECT",VERTEX,{"derivedFrom":[subQ1,subQ0]});Q124=makeQuery(id+"F1.imprint","IMPRINT",FACE,{"disambiguationData":[TD([[makeQuery(id+"F1.imprint","IMPRINT",EDGE,{"disambiguationData":[TD([[subQ2,-1.0]])],"derivedFrom":subQ1}),1.0]])]});}
            var Q125;
            {var subQ0=sQuery(id+"F1.wireOp",EDGE,"E20.bottom");var subQ1=sQuery(id+"F1.wireOp",EDGE,"E12.left");var subQ2=makeQuery(id+"F1.imprint","INTERSECT",VERTEX,{"derivedFrom":[subQ1,subQ0]});Q125=makeQuery(id+"F1.imprint","IMPRINT",FACE,{"disambiguationData":[TD([[makeQuery(id+"F1.imprint","IMPRINT",EDGE,{"disambiguationData":[TD([[subQ2,-1.0]])],"derivedFrom":subQ1}),-1.0]])]});}
            var Q126;
            {var subQ0=sQuery(id+"F1.wireOp",EDGE,"E20.bottom");var subQ1=sQuery(id+"F1.wireOp",EDGE,"E11.right");var subQ2=makeQuery(id+"F1.imprint","INTERSECT",VERTEX,{"derivedFrom":[subQ1,subQ0]});Q126=makeQuery(id+"F1.imprint","IMPRINT",FACE,{"disambiguationData":[TD([[makeQuery(id+"F1.imprint","IMPRINT",EDGE,{"disambiguationData":[TD([[subQ2,-1.0]])],"derivedFrom":subQ1}),-1.0]])]});}
            var Q127;
            {var subQ0=sQuery(id+"F1.wireOp",EDGE,"E20.top");var subQ1=sQuery(id+"F1.wireOp",EDGE,"E12.left");var subQ2=makeQuery(id+"F1.imprint","INTERSECT",VERTEX,{"derivedFrom":[subQ1,subQ0]});Q127=makeQuery(id+"F1.imprint","IMPRINT",FACE,{"disambiguationData":[TD([[makeQuery(id+"F1.imprint","IMPRINT",EDGE,{"disambiguationData":[TD([[subQ2,-1.0]])],"derivedFrom":subQ1}),-1.0]])]});}
            var Q128;
            {var subQ0=sQuery(id+"F1.wireOp",EDGE,"E17.top");var subQ1=sQuery(id+"F1.wireOp",EDGE,"E12.left");var subQ2=makeQuery(id+"F1.imprint","INTERSECT",VERTEX,{"derivedFrom":[subQ1,subQ0]});Q128=makeQuery(id+"F1.imprint","IMPRINT",FACE,{"disambiguationData":[TD([[makeQuery(id+"F1.imprint","IMPRINT",EDGE,{"disambiguationData":[TD([[subQ2,-1.0]])],"derivedFrom":subQ1}),-1.0]])]});}
            var Q129;
            {var subQ0=sQuery(id+"F1.wireOp",EDGE,"E15.top");var subQ1=sQuery(id+"F1.wireOp",EDGE,"E12.left");var subQ2=makeQuery(id+"F1.imprint","INTERSECT",VERTEX,{"derivedFrom":[subQ1,subQ0]});Q129=makeQuery(id+"F1.imprint","IMPRINT",FACE,{"disambiguationData":[TD([[makeQuery(id+"F1.imprint","IMPRINT",EDGE,{"disambiguationData":[TD([[subQ2,-1.0]])],"derivedFrom":subQ1}),-1.0]])]});}
            var Q130;
            {var subQ0=sQuery(id+"F1.wireOp",EDGE,"E17.bottom");var subQ1=sQuery(id+"F1.wireOp",EDGE,"E12.left");var subQ2=makeQuery(id+"F1.imprint","INTERSECT",VERTEX,{"derivedFrom":[subQ1,subQ0]});Q130=makeQuery(id+"F1.imprint","IMPRINT",FACE,{"disambiguationData":[TD([[makeQuery(id+"F1.imprint","IMPRINT",EDGE,{"disambiguationData":[TD([[subQ2,-1.0]])],"derivedFrom":subQ1}),-1.0]])]});}
            var Q131;
            {var subQ0=sQuery(id+"F1.wireOp",EDGE,"E17.bottom");var subQ1=sQuery(id+"F1.wireOp",EDGE,"E11.right");var subQ2=makeQuery(id+"F1.imprint","INTERSECT",VERTEX,{"derivedFrom":[subQ1,subQ0]});Q131=makeQuery(id+"F1.imprint","IMPRINT",FACE,{"disambiguationData":[TD([[makeQuery(id+"F1.imprint","IMPRINT",EDGE,{"disambiguationData":[TD([[subQ2,-1.0]])],"derivedFrom":subQ1}),-1.0]])]});}
            var Q132;
            {var subQ0=sQuery(id+"F1.wireOp",EDGE,"E15.bottom");var subQ1=sQuery(id+"F1.wireOp",EDGE,"E11.right");var subQ2=makeQuery(id+"F1.imprint","INTERSECT",VERTEX,{"derivedFrom":[subQ1,subQ0]});Q132=makeQuery(id+"F1.imprint","IMPRINT",FACE,{"disambiguationData":[TD([[makeQuery(id+"F1.imprint","IMPRINT",EDGE,{"disambiguationData":[TD([[subQ2,-1.0]])],"derivedFrom":subQ1}),-1.0]])]});}
            var Q133;
            {var subQ0=sQuery(id+"F1.wireOp",EDGE,"E16.top");var subQ1=sQuery(id+"F1.wireOp",EDGE,"E11.right");var subQ2=makeQuery(id+"F1.imprint","INTERSECT",VERTEX,{"derivedFrom":[subQ1,subQ0]});Q133=makeQuery(id+"F1.imprint","IMPRINT",FACE,{"disambiguationData":[TD([[makeQuery(id+"F1.imprint","IMPRINT",EDGE,{"disambiguationData":[TD([[subQ2,-1.0]])],"derivedFrom":subQ1}),-1.0]])]});}
            var Q134;
            {var subQ0=sQuery(id+"F1.wireOp",EDGE,"E14.top");var subQ1=sQuery(id+"F1.wireOp",EDGE,"E12.left");var subQ2=makeQuery(id+"F1.imprint","INTERSECT",VERTEX,{"derivedFrom":[subQ1,subQ0]});Q134=makeQuery(id+"F1.imprint","IMPRINT",FACE,{"disambiguationData":[TD([[makeQuery(id+"F1.imprint","IMPRINT",EDGE,{"disambiguationData":[TD([[subQ2,-1.0]])],"derivedFrom":subQ1}),-1.0]])]});}
            var Q135;
            {var subQ0=sQuery(id+"F1.wireOp",EDGE,"E14.top");var subQ1=sQuery(id+"F1.wireOp",EDGE,"E10.left");var subQ2=makeQuery(id+"F1.imprint","INTERSECT",VERTEX,{"derivedFrom":[subQ1,subQ0]});Q135=makeQuery(id+"F1.imprint","IMPRINT",FACE,{"disambiguationData":[TD([[makeQuery(id+"F1.imprint","IMPRINT",EDGE,{"disambiguationData":[TD([[subQ2,-1.0]])],"derivedFrom":subQ1}),1.0]])]});}
            var Q136;
            {var subQ0=sQuery(id+"F1.wireOp",EDGE,"E16.top");var subQ1=sQuery(id+"F1.wireOp",EDGE,"E10.left");var subQ2=makeQuery(id+"F1.imprint","INTERSECT",VERTEX,{"derivedFrom":[subQ1,subQ0]});Q136=makeQuery(id+"F1.imprint","IMPRINT",FACE,{"disambiguationData":[TD([[makeQuery(id+"F1.imprint","IMPRINT",EDGE,{"disambiguationData":[TD([[subQ2,-1.0]])],"derivedFrom":subQ1}),1.0]])]});}
            var Q137;
            {var subQ0=sQuery(id+"F1.wireOp",EDGE,"E16.top");var subQ1=sQuery(id+"F1.wireOp",EDGE,"E9.right");var subQ2=makeQuery(id+"F1.imprint","INTERSECT",VERTEX,{"derivedFrom":[subQ1,subQ0]});Q137=makeQuery(id+"F1.imprint","IMPRINT",FACE,{"disambiguationData":[TD([[makeQuery(id+"F1.imprint","IMPRINT",EDGE,{"disambiguationData":[TD([[subQ2,-1.0]])],"derivedFrom":subQ1}),1.0]])]});}
            var Q138;
            {var subQ0=sQuery(id+"F1.wireOp",EDGE,"E16.top");var subQ1=sQuery(id+"F1.wireOp",EDGE,"E9.left");var subQ2=makeQuery(id+"F1.imprint","INTERSECT",VERTEX,{"derivedFrom":[subQ1,subQ0]});Q138=makeQuery(id+"F1.imprint","IMPRINT",FACE,{"disambiguationData":[TD([[makeQuery(id+"F1.imprint","IMPRINT",EDGE,{"disambiguationData":[TD([[subQ2,-1.0]])],"derivedFrom":subQ1}),1.0]])]});}
            var Q139;
            {var subQ0=sQuery(id+"F1.wireOp",EDGE,"E14.top");var subQ1=sQuery(id+"F1.wireOp",EDGE,"E13.left");var subQ2=makeQuery(id+"F1.imprint","INTERSECT",VERTEX,{"derivedFrom":[subQ1,subQ0]});Q139=makeQuery(id+"F1.imprint","IMPRINT",FACE,{"disambiguationData":[TD([[makeQuery(id+"F1.imprint","IMPRINT",EDGE,{"disambiguationData":[TD([[subQ2,-1.0]])],"derivedFrom":subQ1}),1.0]])]});}
            var Q140;
            {var subQ0=sQuery(id+"F1.wireOp",EDGE,"E18.bottom");var subQ1=sQuery(id+"F1.wireOp",EDGE,"E12.left");var subQ2=makeQuery(id+"F1.imprint","INTERSECT",VERTEX,{"derivedFrom":[subQ1,subQ0]});Q140=makeQuery(id+"F1.imprint","IMPRINT",FACE,{"disambiguationData":[TD([[makeQuery(id+"F1.imprint","IMPRINT",EDGE,{"disambiguationData":[TD([[subQ2,-1.0]])],"derivedFrom":subQ1}),-1.0]])]});}
            var Q141;
            {var subQ0=sQuery(id+"F1.wireOp",EDGE,"E19.top");var subQ1=sQuery(id+"F1.wireOp",EDGE,"E9.left");var subQ2=makeQuery(id+"F1.imprint","INTERSECT",VERTEX,{"derivedFrom":[subQ1,subQ0]});Q141=makeQuery(id+"F1.imprint","IMPRINT",FACE,{"disambiguationData":[TD([[makeQuery(id+"F1.imprint","IMPRINT",EDGE,{"disambiguationData":[TD([[subQ2,-1.0]])],"derivedFrom":subQ1}),1.0]])]});}
            var Q142;
            {var subQ0=sQuery(id+"F1.wireOp",EDGE,"E19.bottom");var subQ1=sQuery(id+"F1.wireOp",EDGE,"E8.right");var subQ2=makeQuery(id+"F1.imprint","INTERSECT",VERTEX,{"derivedFrom":[subQ1,subQ0]});Q142=makeQuery(id+"F1.imprint","IMPRINT",FACE,{"disambiguationData":[TD([[makeQuery(id+"F1.imprint","IMPRINT",EDGE,{"disambiguationData":[TD([[subQ2,-1.0]])],"derivedFrom":subQ1}),1.0]])]});}
            var Q143;
            {var subQ0=sQuery(id+"F1.wireOp",EDGE,"E20.bottom");var subQ1=sQuery(id+"F1.wireOp",EDGE,"E9.left");var subQ2=makeQuery(id+"F1.imprint","INTERSECT",VERTEX,{"derivedFrom":[subQ1,subQ0]});Q143=makeQuery(id+"F1.imprint","IMPRINT",FACE,{"disambiguationData":[TD([[makeQuery(id+"F1.imprint","IMPRINT",EDGE,{"disambiguationData":[TD([[subQ2,-1.0]])],"derivedFrom":subQ1}),1.0]])]});}
            var Q144;
            {var subQ0=sQuery(id+"F1.wireOp",EDGE,"E20.bottom");var subQ1=sQuery(id+"F1.wireOp",EDGE,"E9.right");var subQ2=makeQuery(id+"F1.imprint","INTERSECT",VERTEX,{"derivedFrom":[subQ1,subQ0]});Q144=makeQuery(id+"F1.imprint","IMPRINT",FACE,{"disambiguationData":[TD([[makeQuery(id+"F1.imprint","IMPRINT",EDGE,{"disambiguationData":[TD([[subQ2,-1.0]])],"derivedFrom":subQ1}),1.0]])]});}
            var Q145;
            {var subQ0=sQuery(id+"F1.wireOp",EDGE,"E20.bottom");var subQ1=sQuery(id+"F1.wireOp",EDGE,"E10.left");var subQ2=makeQuery(id+"F1.imprint","INTERSECT",VERTEX,{"derivedFrom":[subQ1,subQ0]});Q145=makeQuery(id+"F1.imprint","IMPRINT",FACE,{"disambiguationData":[TD([[makeQuery(id+"F1.imprint","IMPRINT",EDGE,{"disambiguationData":[TD([[subQ2,-1.0]])],"derivedFrom":subQ1}),1.0]])]});}
            var Q146;
            {var subQ0=sQuery(id+"F1.wireOp",EDGE,"E20.top");var subQ1=sQuery(id+"F1.wireOp",EDGE,"E10.left");var subQ2=makeQuery(id+"F1.imprint","INTERSECT",VERTEX,{"derivedFrom":[subQ1,subQ0]});Q146=makeQuery(id+"F1.imprint","IMPRINT",FACE,{"disambiguationData":[TD([[makeQuery(id+"F1.imprint","IMPRINT",EDGE,{"disambiguationData":[TD([[subQ2,-1.0]])],"derivedFrom":subQ1}),1.0]])]});}
            var Q147;
            {var subQ0=sQuery(id+"F1.wireOp",EDGE,"E21.bottom");var subQ1=sQuery(id+"F1.wireOp",EDGE,"E10.left");var subQ2=makeQuery(id+"F1.imprint","INTERSECT",VERTEX,{"derivedFrom":[subQ1,subQ0]});Q147=makeQuery(id+"F1.imprint","IMPRINT",FACE,{"disambiguationData":[TD([[makeQuery(id+"F1.imprint","IMPRINT",EDGE,{"disambiguationData":[TD([[subQ2,-1.0]])],"derivedFrom":subQ1}),1.0]])]});}
            var Q148;
            {var subQ0=sQuery(id+"F1.wireOp",EDGE,"E21.bottom");var subQ1=sQuery(id+"F1.wireOp",EDGE,"E10.right");var subQ2=makeQuery(id+"F1.imprint","INTERSECT",VERTEX,{"derivedFrom":[subQ1,subQ0]});Q148=makeQuery(id+"F1.imprint","IMPRINT",FACE,{"disambiguationData":[TD([[makeQuery(id+"F1.imprint","IMPRINT",EDGE,{"disambiguationData":[TD([[subQ2,-1.0]])],"derivedFrom":subQ1}),1.0]])]});}
            var Q149;
            {var subQ0=sQuery(id+"F1.wireOp",EDGE,"E21.bottom");var subQ1=sQuery(id+"F1.wireOp",EDGE,"E12.left");var subQ2=makeQuery(id+"F1.imprint","INTERSECT",VERTEX,{"derivedFrom":[subQ1,subQ0]});Q149=makeQuery(id+"F1.imprint","IMPRINT",FACE,{"disambiguationData":[TD([[makeQuery(id+"F1.imprint","IMPRINT",EDGE,{"disambiguationData":[TD([[subQ2,-1.0]])],"derivedFrom":subQ1}),-1.0]])]});}
            var Q150;
            {var subQ0=sQuery(id+"F1.wireOp",EDGE,"E21.bottom");var subQ1=sQuery(id+"F1.wireOp",EDGE,"E11.right");var subQ2=makeQuery(id+"F1.imprint","INTERSECT",VERTEX,{"derivedFrom":[subQ1,subQ0]});Q150=makeQuery(id+"F1.imprint","IMPRINT",FACE,{"disambiguationData":[TD([[makeQuery(id+"F1.imprint","IMPRINT",EDGE,{"disambiguationData":[TD([[subQ2,-1.0]])],"derivedFrom":subQ1}),-1.0]])]});}
            var Q151;
            {var subQ0=sQuery(id+"F1.wireOp",EDGE,"E21.top");var subQ1=sQuery(id+"F1.wireOp",EDGE,"E12.left");var subQ2=makeQuery(id+"F1.imprint","INTERSECT",VERTEX,{"derivedFrom":[subQ1,subQ0]});Q151=makeQuery(id+"F1.imprint","IMPRINT",FACE,{"disambiguationData":[TD([[makeQuery(id+"F1.imprint","IMPRINT",EDGE,{"disambiguationData":[TD([[subQ2,-1.0]])],"derivedFrom":subQ1}),-1.0]])]});}
            var Q152;
            {var subQ0=sQuery(id+"F1.wireOp",EDGE,"E22.bottom");var subQ1=sQuery(id+"F1.wireOp",EDGE,"E12.left");var subQ2=makeQuery(id+"F1.imprint","INTERSECT",VERTEX,{"derivedFrom":[subQ1,subQ0]});Q152=makeQuery(id+"F1.imprint","IMPRINT",FACE,{"disambiguationData":[TD([[makeQuery(id+"F1.imprint","IMPRINT",EDGE,{"disambiguationData":[TD([[subQ2,-1.0]])],"derivedFrom":subQ1}),-1.0]])]});}
            var Q153;
            {var subQ0=sQuery(id+"F1.wireOp",EDGE,"E22.bottom");var subQ1=sQuery(id+"F1.wireOp",EDGE,"E11.right");var subQ2=makeQuery(id+"F1.imprint","INTERSECT",VERTEX,{"derivedFrom":[subQ1,subQ0]});Q153=makeQuery(id+"F1.imprint","IMPRINT",FACE,{"disambiguationData":[TD([[makeQuery(id+"F1.imprint","IMPRINT",EDGE,{"disambiguationData":[TD([[subQ2,-1.0]])],"derivedFrom":subQ1}),-1.0]])]});}
            var Q154;
            {var subQ0=sQuery(id+"F1.wireOp",EDGE,"E22.top");var subQ1=sQuery(id+"F1.wireOp",EDGE,"E12.left");var subQ2=makeQuery(id+"F1.imprint","INTERSECT",VERTEX,{"derivedFrom":[subQ1,subQ0]});Q154=makeQuery(id+"F1.imprint","IMPRINT",FACE,{"disambiguationData":[TD([[makeQuery(id+"F1.imprint","IMPRINT",EDGE,{"disambiguationData":[TD([[subQ2,-1.0]])],"derivedFrom":subQ1}),-1.0]])]});}
            var Q155;
            {var subQ0=sQuery(id+"F1.wireOp",EDGE,"E22.bottom");var subQ1=sQuery(id+"F1.wireOp",EDGE,"E10.right");var subQ2=makeQuery(id+"F1.imprint","INTERSECT",VERTEX,{"derivedFrom":[subQ1,subQ0]});Q155=makeQuery(id+"F1.imprint","IMPRINT",FACE,{"disambiguationData":[TD([[makeQuery(id+"F1.imprint","IMPRINT",EDGE,{"disambiguationData":[TD([[subQ2,-1.0]])],"derivedFrom":subQ1}),1.0]])]});}
            var Q156;
            {var subQ0=sQuery(id+"F1.wireOp",EDGE,"E22.top");var subQ1=sQuery(id+"F1.wireOp",EDGE,"E10.left");var subQ2=makeQuery(id+"F1.imprint","INTERSECT",VERTEX,{"derivedFrom":[subQ1,subQ0]});Q156=makeQuery(id+"F1.imprint","IMPRINT",FACE,{"disambiguationData":[TD([[makeQuery(id+"F1.imprint","IMPRINT",EDGE,{"disambiguationData":[TD([[subQ2,-1.0]])],"derivedFrom":subQ1}),1.0]])]});}
            var Q157;
            {var subQ0=sQuery(id+"F1.wireOp",EDGE,"E22.bottom");var subQ1=sQuery(id+"F1.wireOp",EDGE,"E10.left");var subQ2=makeQuery(id+"F1.imprint","INTERSECT",VERTEX,{"derivedFrom":[subQ1,subQ0]});Q157=makeQuery(id+"F1.imprint","IMPRINT",FACE,{"disambiguationData":[TD([[makeQuery(id+"F1.imprint","IMPRINT",EDGE,{"disambiguationData":[TD([[subQ2,-1.0]])],"derivedFrom":subQ1}),1.0]])]});}
            var Q158;
            {var subQ0=sQuery(id+"F1.wireOp",EDGE,"E21.top");var subQ1=sQuery(id+"F1.wireOp",EDGE,"E10.left");var subQ2=makeQuery(id+"F1.imprint","INTERSECT",VERTEX,{"derivedFrom":[subQ1,subQ0]});Q158=makeQuery(id+"F1.imprint","IMPRINT",FACE,{"disambiguationData":[TD([[makeQuery(id+"F1.imprint","IMPRINT",EDGE,{"disambiguationData":[TD([[subQ2,-1.0]])],"derivedFrom":subQ1}),1.0]])]});}
            var Q159;
            {var subQ0=sQuery(id+"F1.wireOp",EDGE,"E22.bottom");var subQ1=sQuery(id+"F1.wireOp",EDGE,"E9.right");var subQ2=makeQuery(id+"F1.imprint","INTERSECT",VERTEX,{"derivedFrom":[subQ1,subQ0]});Q159=makeQuery(id+"F1.imprint","IMPRINT",FACE,{"disambiguationData":[TD([[makeQuery(id+"F1.imprint","IMPRINT",EDGE,{"disambiguationData":[TD([[subQ2,-1.0]])],"derivedFrom":subQ1}),1.0]])]});}
            var Q160;
            {var subQ0=sQuery(id+"F1.wireOp",EDGE,"E22.bottom");var subQ1=sQuery(id+"F1.wireOp",EDGE,"E9.left");var subQ2=makeQuery(id+"F1.imprint","INTERSECT",VERTEX,{"derivedFrom":[subQ1,subQ0]});Q160=makeQuery(id+"F1.imprint","IMPRINT",FACE,{"disambiguationData":[TD([[makeQuery(id+"F1.imprint","IMPRINT",EDGE,{"disambiguationData":[TD([[subQ2,-1.0]])],"derivedFrom":subQ1}),1.0]])]});}
            var Q161;
            {var subQ0=sQuery(id+"F1.wireOp",EDGE,"E21.top");var subQ1=sQuery(id+"F1.wireOp",EDGE,"E9.left");var subQ2=makeQuery(id+"F1.imprint","INTERSECT",VERTEX,{"derivedFrom":[subQ1,subQ0]});Q161=makeQuery(id+"F1.imprint","IMPRINT",FACE,{"disambiguationData":[TD([[makeQuery(id+"F1.imprint","IMPRINT",EDGE,{"disambiguationData":[TD([[subQ2,-1.0]])],"derivedFrom":subQ1}),1.0]])]});}
            var Q162;
            {var subQ0=sQuery(id+"F1.wireOp",EDGE,"E21.bottom");var subQ1=sQuery(id+"F1.wireOp",EDGE,"E9.left");var subQ2=makeQuery(id+"F1.imprint","INTERSECT",VERTEX,{"derivedFrom":[subQ1,subQ0]});Q162=makeQuery(id+"F1.imprint","IMPRINT",FACE,{"disambiguationData":[TD([[makeQuery(id+"F1.imprint","IMPRINT",EDGE,{"disambiguationData":[TD([[subQ2,-1.0]])],"derivedFrom":subQ1}),1.0]])]});}
            var Q163;
            {var subQ0=sQuery(id+"F1.wireOp",EDGE,"E21.bottom");var subQ1=sQuery(id+"F1.wireOp",EDGE,"E9.right");var subQ2=makeQuery(id+"F1.imprint","INTERSECT",VERTEX,{"derivedFrom":[subQ1,subQ0]});Q163=makeQuery(id+"F1.imprint","IMPRINT",FACE,{"disambiguationData":[TD([[makeQuery(id+"F1.imprint","IMPRINT",EDGE,{"disambiguationData":[TD([[subQ2,-1.0]])],"derivedFrom":subQ1}),1.0]])]});}
            var Q164;
            {var subQ0=sQuery(id+"F1.wireOp",EDGE,"E20.top");var subQ1=sQuery(id+"F1.wireOp",EDGE,"E9.left");var subQ2=makeQuery(id+"F1.imprint","INTERSECT",VERTEX,{"derivedFrom":[subQ1,subQ0]});Q164=makeQuery(id+"F1.imprint","IMPRINT",FACE,{"disambiguationData":[TD([[makeQuery(id+"F1.imprint","IMPRINT",EDGE,{"disambiguationData":[TD([[subQ2,-1.0]])],"derivedFrom":subQ1}),1.0]])]});}
            var Q165;
            {var subQ0=sQuery(id+"F1.wireOp",EDGE,"E20.bottom");var subQ1=sQuery(id+"F1.wireOp",EDGE,"E8.right");var subQ2=makeQuery(id+"F1.imprint","INTERSECT",VERTEX,{"derivedFrom":[subQ1,subQ0]});Q165=makeQuery(id+"F1.imprint","IMPRINT",FACE,{"disambiguationData":[TD([[makeQuery(id+"F1.imprint","IMPRINT",EDGE,{"disambiguationData":[TD([[subQ2,-1.0]])],"derivedFrom":subQ1}),1.0]])]});}
            var Q166;
            {var subQ0=sQuery(id+"F1.wireOp",EDGE,"E19.top");var subQ1=sQuery(id+"F1.wireOp",EDGE,"E8.left");var subQ2=makeQuery(id+"F1.imprint","INTERSECT",VERTEX,{"derivedFrom":[subQ1,subQ0]});Q166=makeQuery(id+"F1.imprint","IMPRINT",FACE,{"disambiguationData":[TD([[makeQuery(id+"F1.imprint","IMPRINT",EDGE,{"disambiguationData":[TD([[subQ2,-1.0]])],"derivedFrom":subQ1}),1.0]])]});}
            var Q167;
            {var subQ0=sQuery(id+"F1.wireOp",EDGE,"E19.bottom");var subQ1=sQuery(id+"F1.wireOp",EDGE,"E9.left");var subQ2=makeQuery(id+"F1.imprint","INTERSECT",VERTEX,{"derivedFrom":[subQ1,subQ0]});Q167=makeQuery(id+"F1.imprint","IMPRINT",FACE,{"disambiguationData":[TD([[makeQuery(id+"F1.imprint","IMPRINT",EDGE,{"disambiguationData":[TD([[subQ2,-1.0]])],"derivedFrom":subQ1}),1.0]])]});}
            var Q168;
            {var subQ0=sQuery(id+"F1.wireOp",EDGE,"E22.top");var subQ1=sQuery(id+"F1.wireOp",EDGE,"E9.left");var subQ2=makeQuery(id+"F1.imprint","INTERSECT",VERTEX,{"derivedFrom":[subQ1,subQ0]});Q168=makeQuery(id+"F1.imprint","IMPRINT",FACE,{"disambiguationData":[TD([[makeQuery(id+"F1.imprint","IMPRINT",EDGE,{"disambiguationData":[TD([[subQ2,-1.0]])],"derivedFrom":subQ1}),1.0]])]});}
            var Q169;
            {var subQ0=sQuery(id+"F1.wireOp",EDGE,"E22.bottom");var subQ1=sQuery(id+"F1.wireOp",EDGE,"E8.right");var subQ2=makeQuery(id+"F1.imprint","INTERSECT",VERTEX,{"derivedFrom":[subQ1,subQ0]});Q169=makeQuery(id+"F1.imprint","IMPRINT",FACE,{"disambiguationData":[TD([[makeQuery(id+"F1.imprint","IMPRINT",EDGE,{"disambiguationData":[TD([[subQ2,-1.0]])],"derivedFrom":subQ1}),1.0]])]});}
            var Q170;
            {var subQ0=sQuery(id+"F1.wireOp",EDGE,"E21.top");var subQ1=sQuery(id+"F1.wireOp",EDGE,"E8.left");var subQ2=makeQuery(id+"F1.imprint","INTERSECT",VERTEX,{"derivedFrom":[subQ1,subQ0]});Q170=makeQuery(id+"F1.imprint","IMPRINT",FACE,{"disambiguationData":[TD([[makeQuery(id+"F1.imprint","IMPRINT",EDGE,{"disambiguationData":[TD([[subQ2,-1.0]])],"derivedFrom":subQ1}),1.0]])]});}
            var Q171;
            {var subQ0=sQuery(id+"F1.wireOp",EDGE,"E22.bottom");var subQ1=sQuery(id+"F1.wireOp",EDGE,"E8.left");var subQ2=makeQuery(id+"F1.imprint","INTERSECT",VERTEX,{"derivedFrom":[subQ1,subQ0]});Q171=makeQuery(id+"F1.imprint","IMPRINT",FACE,{"disambiguationData":[TD([[makeQuery(id+"F1.imprint","IMPRINT",EDGE,{"disambiguationData":[TD([[subQ2,-1.0]])],"derivedFrom":subQ1}),1.0]])]});}
            var Q172;
            {var subQ0=sQuery(id+"F1.wireOp",EDGE,"E22.top");var subQ1=sQuery(id+"F1.wireOp",EDGE,"E8.left");var subQ2=makeQuery(id+"F1.imprint","INTERSECT",VERTEX,{"derivedFrom":[subQ1,subQ0]});Q172=makeQuery(id+"F1.imprint","IMPRINT",FACE,{"disambiguationData":[TD([[makeQuery(id+"F1.imprint","IMPRINT",EDGE,{"disambiguationData":[TD([[subQ2,-1.0]])],"derivedFrom":subQ1}),1.0]])]});}
            var Q173;
            {var subQ0=sQuery(id+"F1.wireOp",EDGE,"E22.bottom");var subQ1=sQuery(id+"F1.wireOp",EDGE,"E8.left");var subQ2=makeQuery(id+"F1.imprint","INTERSECT",VERTEX,{"derivedFrom":[subQ1,subQ0]});Q173=makeQuery(id+"F1.imprint","IMPRINT",FACE,{"disambiguationData":[TD([[makeQuery(id+"F1.imprint","IMPRINT",EDGE,{"disambiguationData":[TD([[subQ2,-1.0]])],"derivedFrom":subQ1}),-1.0]])]});}
            var Q174;
            {var subQ0=sQuery(id+"F1.wireOp",EDGE,"E21.bottom");var subQ1=sQuery(id+"F1.wireOp",EDGE,"E8.left");var subQ2=makeQuery(id+"F1.imprint","INTERSECT",VERTEX,{"derivedFrom":[subQ1,subQ0]});Q174=makeQuery(id+"F1.imprint","IMPRINT",FACE,{"disambiguationData":[TD([[makeQuery(id+"F1.imprint","IMPRINT",EDGE,{"disambiguationData":[TD([[subQ2,-1.0]])],"derivedFrom":subQ1}),-1.0]])]});}
            var Q175;
            {var subQ0=sQuery(id+"F1.wireOp",EDGE,"E21.bottom");var subQ1=sQuery(id+"F1.wireOp",EDGE,"E8.left");var subQ2=makeQuery(id+"F1.imprint","INTERSECT",VERTEX,{"derivedFrom":[subQ1,subQ0]});Q175=makeQuery(id+"F1.imprint","IMPRINT",FACE,{"disambiguationData":[TD([[makeQuery(id+"F1.imprint","IMPRINT",EDGE,{"disambiguationData":[TD([[subQ2,-1.0]])],"derivedFrom":subQ1}),1.0]])]});}
            var Q176;
            {var subQ0=sQuery(id+"F1.wireOp",EDGE,"E21.bottom");var subQ1=sQuery(id+"F1.wireOp",EDGE,"E8.right");var subQ2=makeQuery(id+"F1.imprint","INTERSECT",VERTEX,{"derivedFrom":[subQ1,subQ0]});Q176=makeQuery(id+"F1.imprint","IMPRINT",FACE,{"disambiguationData":[TD([[makeQuery(id+"F1.imprint","IMPRINT",EDGE,{"disambiguationData":[TD([[subQ2,-1.0]])],"derivedFrom":subQ1}),1.0]])]});}
            var Q177;
            {var subQ0=sQuery(id+"F1.wireOp",EDGE,"E20.top");var subQ1=sQuery(id+"F1.wireOp",EDGE,"E8.left");var subQ2=makeQuery(id+"F1.imprint","INTERSECT",VERTEX,{"derivedFrom":[subQ1,subQ0]});Q177=makeQuery(id+"F1.imprint","IMPRINT",FACE,{"disambiguationData":[TD([[makeQuery(id+"F1.imprint","IMPRINT",EDGE,{"disambiguationData":[TD([[subQ2,-1.0]])],"derivedFrom":subQ1}),1.0]])]});}
            var Q178;
            {var subQ0=sQuery(id+"F1.wireOp",EDGE,"E20.bottom");var subQ1=sQuery(id+"F1.wireOp",EDGE,"E8.left");var subQ2=makeQuery(id+"F1.imprint","INTERSECT",VERTEX,{"derivedFrom":[subQ1,subQ0]});Q178=makeQuery(id+"F1.imprint","IMPRINT",FACE,{"disambiguationData":[TD([[makeQuery(id+"F1.imprint","IMPRINT",EDGE,{"disambiguationData":[TD([[subQ2,-1.0]])],"derivedFrom":subQ1}),1.0]])]});}
            var Q179;
            {var subQ0=sQuery(id+"F1.wireOp",EDGE,"E20.bottom");var subQ1=sQuery(id+"F1.wireOp",EDGE,"E8.left");var subQ2=makeQuery(id+"F1.imprint","INTERSECT",VERTEX,{"derivedFrom":[subQ1,subQ0]});Q179=makeQuery(id+"F1.imprint","IMPRINT",FACE,{"disambiguationData":[TD([[makeQuery(id+"F1.imprint","IMPRINT",EDGE,{"disambiguationData":[TD([[subQ2,-1.0]])],"derivedFrom":subQ1}),-1.0]])]});}
            var Q180;
            {var subQ0=sQuery(id+"F1.wireOp",EDGE,"E19.top");var subQ1=sQuery(id+"F1.wireOp",EDGE,"E13.left");var subQ2=makeQuery(id+"F1.imprint","INTERSECT",VERTEX,{"derivedFrom":[subQ1,subQ0]});Q180=makeQuery(id+"F1.imprint","IMPRINT",FACE,{"disambiguationData":[TD([[makeQuery(id+"F1.imprint","IMPRINT",EDGE,{"disambiguationData":[TD([[subQ2,-1.0]])],"derivedFrom":subQ1}),1.0]])]});}
            var Q181;
            {var subQ0=sQuery(id+"F1.wireOp",EDGE,"E20.bottom");var subQ1=sQuery(id+"F1.wireOp",EDGE,"E13.left");var subQ2=makeQuery(id+"F1.imprint","INTERSECT",VERTEX,{"derivedFrom":[subQ1,subQ0]});Q181=makeQuery(id+"F1.imprint","IMPRINT",FACE,{"disambiguationData":[TD([[makeQuery(id+"F1.imprint","IMPRINT",EDGE,{"disambiguationData":[TD([[subQ2,-1.0]])],"derivedFrom":subQ1}),1.0]])]});}
            var Q182;
            {var subQ0=sQuery(id+"F1.wireOp",EDGE,"E20.top");var subQ1=sQuery(id+"F1.wireOp",EDGE,"E13.left");var subQ2=makeQuery(id+"F1.imprint","INTERSECT",VERTEX,{"derivedFrom":[subQ1,subQ0]});Q182=makeQuery(id+"F1.imprint","IMPRINT",FACE,{"disambiguationData":[TD([[makeQuery(id+"F1.imprint","IMPRINT",EDGE,{"disambiguationData":[TD([[subQ2,-1.0]])],"derivedFrom":subQ1}),1.0]])]});}
            var Q183;
            {var subQ0=sQuery(id+"F1.wireOp",EDGE,"E21.bottom");var subQ1=sQuery(id+"F1.wireOp",EDGE,"E13.left");var subQ2=makeQuery(id+"F1.imprint","INTERSECT",VERTEX,{"derivedFrom":[subQ1,subQ0]});Q183=makeQuery(id+"F1.imprint","IMPRINT",FACE,{"disambiguationData":[TD([[makeQuery(id+"F1.imprint","IMPRINT",EDGE,{"disambiguationData":[TD([[subQ2,-1.0]])],"derivedFrom":subQ1}),1.0]])]});}
            var Q184;
            {var subQ0=sQuery(id+"F1.wireOp",EDGE,"E21.top");var subQ1=sQuery(id+"F1.wireOp",EDGE,"E13.left");var subQ2=makeQuery(id+"F1.imprint","INTERSECT",VERTEX,{"derivedFrom":[subQ1,subQ0]});Q184=makeQuery(id+"F1.imprint","IMPRINT",FACE,{"disambiguationData":[TD([[makeQuery(id+"F1.imprint","IMPRINT",EDGE,{"disambiguationData":[TD([[subQ2,-1.0]])],"derivedFrom":subQ1}),1.0]])]});}
            var Q185;
            {var subQ0=sQuery(id+"F1.wireOp",EDGE,"E22.bottom");var subQ1=sQuery(id+"F1.wireOp",EDGE,"E13.left");var subQ2=makeQuery(id+"F1.imprint","INTERSECT",VERTEX,{"derivedFrom":[subQ1,subQ0]});Q185=makeQuery(id+"F1.imprint","IMPRINT",FACE,{"disambiguationData":[TD([[makeQuery(id+"F1.imprint","IMPRINT",EDGE,{"disambiguationData":[TD([[subQ2,-1.0]])],"derivedFrom":subQ1}),1.0]])]});}
            var Q186;
            {var subQ0=sQuery(id+"F1.wireOp",EDGE,"E22.top");var subQ1=sQuery(id+"F1.wireOp",EDGE,"E13.left");var subQ2=makeQuery(id+"F1.imprint","INTERSECT",VERTEX,{"derivedFrom":[subQ1,subQ0]});Q186=makeQuery(id+"F1.imprint","IMPRINT",FACE,{"disambiguationData":[TD([[makeQuery(id+"F1.imprint","IMPRINT",EDGE,{"disambiguationData":[TD([[subQ2,-1.0]])],"derivedFrom":subQ1}),1.0]])]});}
            var Q187;
            {var subQ0=sQuery(id+"F1.wireOp",EDGE,"E22.bottom");var subQ1=sQuery(id+"F1.wireOp",EDGE,"E7.right");var subQ2=makeQuery(id+"F1.imprint","INTERSECT",VERTEX,{"derivedFrom":[subQ1,subQ0]});Q187=makeQuery(id+"F1.imprint","IMPRINT",FACE,{"disambiguationData":[TD([[makeQuery(id+"F1.imprint","IMPRINT",EDGE,{"disambiguationData":[TD([[subQ2,-1.0]])],"derivedFrom":subQ1}),1.0]])]});}
            var Q188;
            {var subQ0=sQuery(id+"F1.wireOp",EDGE,"E22.top");var subQ1=sQuery(id+"F1.wireOp",EDGE,"E7.left");var subQ2=makeQuery(id+"F1.imprint","INTERSECT",VERTEX,{"derivedFrom":[subQ1,subQ0]});Q188=makeQuery(id+"F1.imprint","IMPRINT",FACE,{"disambiguationData":[TD([[makeQuery(id+"F1.imprint","IMPRINT",EDGE,{"disambiguationData":[TD([[subQ2,-1.0]])],"derivedFrom":subQ1}),1.0]])]});}
            var Q189;
            {var subQ0=sQuery(id+"F1.wireOp",EDGE,"E22.bottom");var subQ1=sQuery(id+"F1.wireOp",EDGE,"E7.left");var subQ2=makeQuery(id+"F1.imprint","INTERSECT",VERTEX,{"derivedFrom":[subQ1,subQ0]});Q189=makeQuery(id+"F1.imprint","IMPRINT",FACE,{"disambiguationData":[TD([[makeQuery(id+"F1.imprint","IMPRINT",EDGE,{"disambiguationData":[TD([[subQ2,-1.0]])],"derivedFrom":subQ1}),1.0]])]});}
            var Q190;
            {var subQ0=sQuery(id+"F1.wireOp",EDGE,"E22.bottom");var subQ1=sQuery(id+"F1.wireOp",EDGE,"E6.right");var subQ2=makeQuery(id+"F1.imprint","INTERSECT",VERTEX,{"derivedFrom":[subQ1,subQ0]});Q190=makeQuery(id+"F1.imprint","IMPRINT",FACE,{"disambiguationData":[TD([[makeQuery(id+"F1.imprint","IMPRINT",EDGE,{"disambiguationData":[TD([[subQ2,-1.0]])],"derivedFrom":subQ1}),1.0]])]});}
            var Q191;
            {var subQ0=sQuery(id+"F1.wireOp",EDGE,"E21.top");var subQ1=sQuery(id+"F1.wireOp",EDGE,"E7.left");var subQ2=makeQuery(id+"F1.imprint","INTERSECT",VERTEX,{"derivedFrom":[subQ1,subQ0]});Q191=makeQuery(id+"F1.imprint","IMPRINT",FACE,{"disambiguationData":[TD([[makeQuery(id+"F1.imprint","IMPRINT",EDGE,{"disambiguationData":[TD([[subQ2,-1.0]])],"derivedFrom":subQ1}),1.0]])]});}
            var Q192;
            {var subQ0=sQuery(id+"F1.wireOp",EDGE,"E21.bottom");var subQ1=sQuery(id+"F1.wireOp",EDGE,"E7.right");var subQ2=makeQuery(id+"F1.imprint","INTERSECT",VERTEX,{"derivedFrom":[subQ1,subQ0]});Q192=makeQuery(id+"F1.imprint","IMPRINT",FACE,{"disambiguationData":[TD([[makeQuery(id+"F1.imprint","IMPRINT",EDGE,{"disambiguationData":[TD([[subQ2,-1.0]])],"derivedFrom":subQ1}),1.0]])]});}
            var Q193;
            {var subQ0=sQuery(id+"F1.wireOp",EDGE,"E21.bottom");var subQ1=sQuery(id+"F1.wireOp",EDGE,"E7.left");var subQ2=makeQuery(id+"F1.imprint","INTERSECT",VERTEX,{"derivedFrom":[subQ1,subQ0]});Q193=makeQuery(id+"F1.imprint","IMPRINT",FACE,{"disambiguationData":[TD([[makeQuery(id+"F1.imprint","IMPRINT",EDGE,{"disambiguationData":[TD([[subQ2,-1.0]])],"derivedFrom":subQ1}),1.0]])]});}
            var Q194;
            {var subQ0=sQuery(id+"F1.wireOp",EDGE,"E20.top");var subQ1=sQuery(id+"F1.wireOp",EDGE,"E7.left");var subQ2=makeQuery(id+"F1.imprint","INTERSECT",VERTEX,{"derivedFrom":[subQ1,subQ0]});Q194=makeQuery(id+"F1.imprint","IMPRINT",FACE,{"disambiguationData":[TD([[makeQuery(id+"F1.imprint","IMPRINT",EDGE,{"disambiguationData":[TD([[subQ2,-1.0]])],"derivedFrom":subQ1}),1.0]])]});}
            var Q195;
            {var subQ0=sQuery(id+"F1.wireOp",EDGE,"E20.bottom");var subQ1=sQuery(id+"F1.wireOp",EDGE,"E7.right");var subQ2=makeQuery(id+"F1.imprint","INTERSECT",VERTEX,{"derivedFrom":[subQ1,subQ0]});Q195=makeQuery(id+"F1.imprint","IMPRINT",FACE,{"disambiguationData":[TD([[makeQuery(id+"F1.imprint","IMPRINT",EDGE,{"disambiguationData":[TD([[subQ2,-1.0]])],"derivedFrom":subQ1}),1.0]])]});}
            var Q196;
            {var subQ0=sQuery(id+"F1.wireOp",EDGE,"E20.bottom");var subQ1=sQuery(id+"F1.wireOp",EDGE,"E7.left");var subQ2=makeQuery(id+"F1.imprint","INTERSECT",VERTEX,{"derivedFrom":[subQ1,subQ0]});Q196=makeQuery(id+"F1.imprint","IMPRINT",FACE,{"disambiguationData":[TD([[makeQuery(id+"F1.imprint","IMPRINT",EDGE,{"disambiguationData":[TD([[subQ2,-1.0]])],"derivedFrom":subQ1}),1.0]])]});}
            var Q197;
            {var subQ0=sQuery(id+"F1.wireOp",EDGE,"E19.top");var subQ1=sQuery(id+"F1.wireOp",EDGE,"E7.left");var subQ2=makeQuery(id+"F1.imprint","INTERSECT",VERTEX,{"derivedFrom":[subQ1,subQ0]});Q197=makeQuery(id+"F1.imprint","IMPRINT",FACE,{"disambiguationData":[TD([[makeQuery(id+"F1.imprint","IMPRINT",EDGE,{"disambiguationData":[TD([[subQ2,-1.0]])],"derivedFrom":subQ1}),1.0]])]});}
            var Q198;
            {var subQ0=sQuery(id+"F1.wireOp",EDGE,"E20.bottom");var subQ1=sQuery(id+"F1.wireOp",EDGE,"E6.right");var subQ2=makeQuery(id+"F1.imprint","INTERSECT",VERTEX,{"derivedFrom":[subQ1,subQ0]});Q198=makeQuery(id+"F1.imprint","IMPRINT",FACE,{"disambiguationData":[TD([[makeQuery(id+"F1.imprint","IMPRINT",EDGE,{"disambiguationData":[TD([[subQ2,-1.0]])],"derivedFrom":subQ1}),1.0]])]});}
            var Q199;
            {var subQ0=sQuery(id+"F1.wireOp",EDGE,"E20.bottom");var subQ1=sQuery(id+"F1.wireOp",EDGE,"E6.left");var subQ2=makeQuery(id+"F1.imprint","INTERSECT",VERTEX,{"derivedFrom":[subQ1,subQ0]});Q199=makeQuery(id+"F1.imprint","IMPRINT",FACE,{"disambiguationData":[TD([[makeQuery(id+"F1.imprint","IMPRINT",EDGE,{"disambiguationData":[TD([[subQ2,-1.0]])],"derivedFrom":subQ1}),1.0]])]});}
            var Q200;
            {var subQ0=sQuery(id+"F1.wireOp",EDGE,"E20.top");var subQ1=sQuery(id+"F1.wireOp",EDGE,"E6.left");var subQ2=makeQuery(id+"F1.imprint","INTERSECT",VERTEX,{"derivedFrom":[subQ1,subQ0]});Q200=makeQuery(id+"F1.imprint","IMPRINT",FACE,{"disambiguationData":[TD([[makeQuery(id+"F1.imprint","IMPRINT",EDGE,{"disambiguationData":[TD([[subQ2,-1.0]])],"derivedFrom":subQ1}),1.0]])]});}
            var Q201;
            {var subQ0=sQuery(id+"F1.wireOp",EDGE,"E21.bottom");var subQ1=sQuery(id+"F1.wireOp",EDGE,"E6.left");var subQ2=makeQuery(id+"F1.imprint","INTERSECT",VERTEX,{"derivedFrom":[subQ1,subQ0]});Q201=makeQuery(id+"F1.imprint","IMPRINT",FACE,{"disambiguationData":[TD([[makeQuery(id+"F1.imprint","IMPRINT",EDGE,{"disambiguationData":[TD([[subQ2,-1.0]])],"derivedFrom":subQ1}),1.0]])]});}
            var Q202;
            {var subQ0=sQuery(id+"F1.wireOp",EDGE,"E21.bottom");var subQ1=sQuery(id+"F1.wireOp",EDGE,"E6.right");var subQ2=makeQuery(id+"F1.imprint","INTERSECT",VERTEX,{"derivedFrom":[subQ1,subQ0]});Q202=makeQuery(id+"F1.imprint","IMPRINT",FACE,{"disambiguationData":[TD([[makeQuery(id+"F1.imprint","IMPRINT",EDGE,{"disambiguationData":[TD([[subQ2,-1.0]])],"derivedFrom":subQ1}),1.0]])]});}
            var Q203;
            {var subQ0=sQuery(id+"F1.wireOp",EDGE,"E21.bottom");var subQ1=sQuery(id+"F1.wireOp",EDGE,"E5.right");var subQ2=makeQuery(id+"F1.imprint","INTERSECT",VERTEX,{"derivedFrom":[subQ1,subQ0]});Q203=makeQuery(id+"F1.imprint","IMPRINT",FACE,{"disambiguationData":[TD([[makeQuery(id+"F1.imprint","IMPRINT",EDGE,{"disambiguationData":[TD([[subQ2,-1.0]])],"derivedFrom":subQ1}),1.0]])]});}
            var Q204;
            {var subQ0=sQuery(id+"F1.wireOp",EDGE,"E20.bottom");var subQ1=sQuery(id+"F1.wireOp",EDGE,"E5.right");var subQ2=makeQuery(id+"F1.imprint","INTERSECT",VERTEX,{"derivedFrom":[subQ1,subQ0]});Q204=makeQuery(id+"F1.imprint","IMPRINT",FACE,{"disambiguationData":[TD([[makeQuery(id+"F1.imprint","IMPRINT",EDGE,{"disambiguationData":[TD([[subQ2,-1.0]])],"derivedFrom":subQ1}),1.0]])]});}
            var Q205;
            {var subQ0=sQuery(id+"F1.wireOp",EDGE,"E20.bottom");var subQ1=sQuery(id+"F1.wireOp",EDGE,"E5.left");var subQ2=makeQuery(id+"F1.imprint","INTERSECT",VERTEX,{"derivedFrom":[subQ1,subQ0]});Q205=makeQuery(id+"F1.imprint","IMPRINT",FACE,{"disambiguationData":[TD([[makeQuery(id+"F1.imprint","IMPRINT",EDGE,{"disambiguationData":[TD([[subQ2,-1.0]])],"derivedFrom":subQ1}),1.0]])]});}
            var Q206;
            {var subQ0=sQuery(id+"F1.wireOp",EDGE,"E21.bottom");var subQ1=sQuery(id+"F1.wireOp",EDGE,"E5.left");var subQ2=makeQuery(id+"F1.imprint","INTERSECT",VERTEX,{"derivedFrom":[subQ1,subQ0]});Q206=makeQuery(id+"F1.imprint","IMPRINT",FACE,{"disambiguationData":[TD([[makeQuery(id+"F1.imprint","IMPRINT",EDGE,{"disambiguationData":[TD([[subQ2,-1.0]])],"derivedFrom":subQ1}),1.0]])]});}
            var Q207;
            {var subQ0=sQuery(id+"F1.wireOp",EDGE,"E22.bottom");var subQ1=sQuery(id+"F1.wireOp",EDGE,"E6.left");var subQ2=makeQuery(id+"F1.imprint","INTERSECT",VERTEX,{"derivedFrom":[subQ1,subQ0]});Q207=makeQuery(id+"F1.imprint","IMPRINT",FACE,{"disambiguationData":[TD([[makeQuery(id+"F1.imprint","IMPRINT",EDGE,{"disambiguationData":[TD([[subQ2,-1.0]])],"derivedFrom":subQ1}),1.0]])]});}
            var Q208;
            {var subQ0=sQuery(id+"F1.wireOp",EDGE,"E22.bottom");var subQ1=sQuery(id+"F1.wireOp",EDGE,"E5.left");var subQ2=makeQuery(id+"F1.imprint","INTERSECT",VERTEX,{"derivedFrom":[subQ1,subQ0]});Q208=makeQuery(id+"F1.imprint","IMPRINT",FACE,{"disambiguationData":[TD([[makeQuery(id+"F1.imprint","IMPRINT",EDGE,{"disambiguationData":[TD([[subQ2,-1.0]])],"derivedFrom":subQ1}),1.0]])]});}
            extrude(context, id + "F2", {"entities" : qUnion([Q0, Q1, Q2, Q3, Q4, Q5, Q6, Q7, Q8, Q9, Q10, Q11, Q12, Q13, Q14, Q15, Q16, Q17, Q18, Q19, Q20, Q21, Q22, Q23, Q24, Q25, Q26, Q27, Q28, Q29, Q30, Q31, Q32, Q33, Q34, Q35, Q36, Q37, Q38, Q39, Q40, Q41, Q42, Q43, Q44, Q45, Q46, Q47, Q48, Q49, Q50, Q51, Q52, Q53, Q54, Q55, Q56, Q57, Q58, Q59, Q60, Q61, Q62, Q63, Q64, Q65, Q66, Q67, Q68, Q69, Q70, Q71, Q72, Q73, Q74, Q75, Q76, Q77, Q78, Q79, Q80, Q81, Q82, Q83, Q84, Q85, Q86, Q87, Q88, Q89, Q90, Q91, Q92, Q93, Q94, Q95, Q96, Q97, Q98, Q99, Q100, Q101, Q102, Q103, Q104, Q105, Q106, Q107, Q108, Q109, Q110, Q111, Q112, Q113, Q114, Q115, Q116, Q117, Q118, Q119, Q120, Q121, Q122, Q123, Q124, Q125, Q126, Q127, Q128, Q129, Q130, Q131, Q132, Q133, Q134, Q135, Q136, Q137, Q138, Q139, Q140, Q141, Q142, Q143, Q144, Q145, Q146, Q147, Q148, Q149, Q150, Q151, Q152, Q153, Q154, Q155, Q156, Q157, Q158, Q159, Q160, Q161, Q162, Q163, Q164, Q165, Q166, Q167, Q168, Q169, Q170, Q171, Q172, Q173, Q174, Q175, Q176, Q177, Q178, Q179, Q180, Q181, Q182, Q183, Q184, Q185, Q186, Q187, Q188, Q189, Q190, Q191, Q192, Q193, Q194, Q195, Q196, Q197, Q198, Q199, Q200, Q201, Q202, Q203, Q204, Q205, Q206, Q207, Q208]), "depth" : (getVariable(context, 'Diameter')) * mm, "offsetDistance" : 25.4 * mm});
        }
    });
